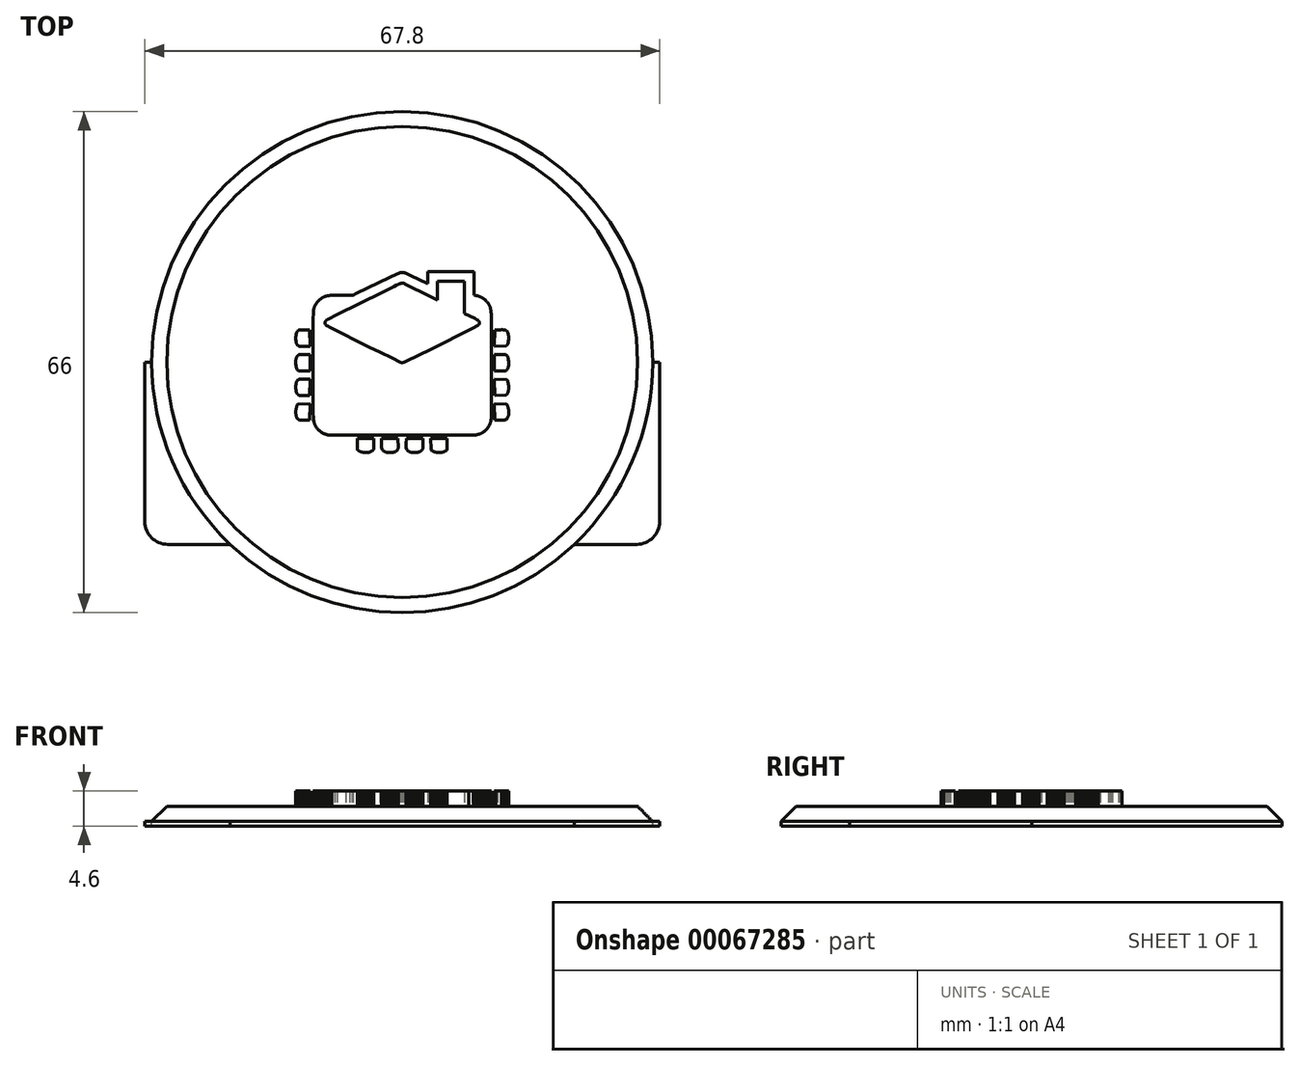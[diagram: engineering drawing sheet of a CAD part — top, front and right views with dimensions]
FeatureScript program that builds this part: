
annotation { "Feature Type Name" : "Feature", "Feature Type Description" : "" }
export const myFeature = defineFeature(function(context is Context, id is Id, definition is map)
    precondition{}
    {
        {
            var Q0;
            Q0=qCreatedBy(makeId("Top.planeOp"),FACE);
            var sketch = newSketch(context, id + "F0", { "sketchPlane" : qUnion([Q0])});
            skCircle(sketch, "E0", {"center": v(0, 0) * mm, "radius": 33 * mm});
            skLineSegment(sketch, "E1", {"start": v(0, -33) * mm, "end": v(0, -24) * mm});
            skLineSegment(sketch, "E2", {"start": v(0, -24) * mm, "end": v(33.9, -24) * mm});
            skLineSegment(sketch, "E3", {"start": v(33.9, -24) * mm, "end": v(33.9, 0) * mm});
            skLineSegment(sketch, "E4", {"start": v(33.9, 0) * mm, "end": v(33, 0) * mm});
            skLineSegment(sketch, "E5.MirrorCS", {"start": v(0, -24) * mm, "end": v(-33.9, -24) * mm});
            skLineSegment(sketch, "E6.MirrorCS", {"start": v(-33.9, 0) * mm, "end": v(-33, 0) * mm});
            skLineSegment(sketch, "E7.MirrorCS", {"start": v(-33.9, -24) * mm, "end": v(-33.9, 0) * mm});
            skSolve(sketch);
        }
        {
            var Q0;
            {var subQ0=sQuery(id+"F0.wireOp",EDGE,"E1");Q0=makeQuery(id+"F0.imprint","IMPRINT",FACE,{"disambiguationData":[TD([[makeQuery(id+"F0.imprint","IMPRINT",EDGE,{"derivedFrom":subQ0}),1.0]])]});}
            var Q1;
            {var subQ0=sQuery(id+"F0.wireOp",EDGE,"E1");Q1=makeQuery(id+"F0.imprint","IMPRINT",FACE,{"disambiguationData":[TD([[makeQuery(id+"F0.imprint","IMPRINT",EDGE,{"derivedFrom":subQ0}),-1.0]])]});}
            var Q2;
            {var subQ3=sQuery(id+"F0.wireOp",EDGE,"E0");var subQ5=makeQuery(id+"F0.imprint","INTERSECT",VERTEX,{"derivedFrom":[subQ3,sQuery(id+"F0.wireOp",EDGE,"E4")]});Q2=makeQuery(id+"F0.imprint","IMPRINT",FACE,{"disambiguationData":[TD([[makeQuery(id+"F0.imprint","IMPRINT",EDGE,{"disambiguationData":[TD([[subQ5,-1.0]])],"derivedFrom":subQ3}),1.0]])]});}
            var Q3;
            {var subQ0=sQuery(id+"F0.wireOp",EDGE,"E6.MirrorCS");Q3=makeQuery(id+"F0.imprint","IMPRINT",FACE,{"disambiguationData":[TD([[makeQuery(id+"F0.imprint","IMPRINT",EDGE,{"derivedFrom":subQ0}),-1.0]])]});}
            var Q4;
            {var subQ4=sQuery(id+"F0.wireOp",EDGE,"E3");Q4=makeQuery(id+"F0.imprint","IMPRINT",FACE,{"disambiguationData":[TD([[makeQuery(id+"F0.imprint","IMPRINT",EDGE,{"derivedFrom":subQ4}),1.0]])]});}
            extrude(context, id + "F1", {"entities" : qUnion([Q0, Q1, Q2, Q3, Q4]), "oppositeDirection" : true, "depth" : 0.6 * mm});
        }
        {
            var Q0;
            {var subQ3=sQuery(id+"F0.wireOp",EDGE,"E0");var subQ5=makeQuery(id+"F0.imprint","INTERSECT",VERTEX,{"derivedFrom":[subQ3,sQuery(id+"F0.wireOp",EDGE,"E4")]});Q0=makeQuery(id+"F0.imprint","IMPRINT",FACE,{"disambiguationData":[TD([[makeQuery(id+"F0.imprint","IMPRINT",EDGE,{"disambiguationData":[TD([[subQ5,-1.0]])],"derivedFrom":subQ3}),1.0]])]});}
            var Q1;
            {var subQ0=sQuery(id+"F0.wireOp",EDGE,"E1");Q1=makeQuery(id+"F0.imprint","IMPRINT",FACE,{"disambiguationData":[TD([[makeQuery(id+"F0.imprint","IMPRINT",EDGE,{"derivedFrom":subQ0}),1.0]])]});}
            var Q2;
            {var subQ0=sQuery(id+"F0.wireOp",EDGE,"E1");Q2=makeQuery(id+"F0.imprint","IMPRINT",FACE,{"disambiguationData":[TD([[makeQuery(id+"F0.imprint","IMPRINT",EDGE,{"derivedFrom":subQ0}),-1.0]])]});}
            extrude(context, id + "F2", {"entities" : qUnion([Q0, Q1, Q2]), "operationType" : NewBodyOperationType.ADD, "depth" : 2 * mm, "hasDraft" : true, "draftAngle" : 45 * degree, "draftPullDirection" : true});
        }
        {
            var Q0;
            Q0=qCreatedBy(makeId("Top.planeOp"),FACE);
            var sketch = newSketch(context, id + "F3", { "sketchPlane" : qUnion([Q0])});
            skLineSegment(sketch, "E8", {"start": v(3.39, 11.92) * mm, "end": v(9.43, 11.9) * mm});
            skLineSegment(sketch, "E9", {"start": v(9.43, 11.9) * mm, "end": v(9.45, 8.81) * mm});
            skLineSegment(sketch, "E10", {"start": v(9.45, 8.81) * mm, "end": v(9.52, 8.8) * mm});
            skLineSegment(sketch, "E11", {"start": v(9.52, 8.8) * mm, "end": v(9.6, 8.8) * mm});
            skLineSegment(sketch, "E12", {"start": v(9.6, 8.8) * mm, "end": v(9.66, 8.78) * mm});
            skLineSegment(sketch, "E13", {"start": v(9.66, 8.78) * mm, "end": v(9.73, 8.77) * mm});
            skLineSegment(sketch, "E14", {"start": v(9.73, 8.77) * mm, "end": v(9.8, 8.75) * mm});
            skLineSegment(sketch, "E15", {"start": v(9.8, 8.75) * mm, "end": v(9.88, 8.73) * mm});
            skLineSegment(sketch, "E16", {"start": v(9.88, 8.73) * mm, "end": v(9.95, 8.71) * mm});
            skLineSegment(sketch, "E17", {"start": v(9.95, 8.71) * mm, "end": v(10.02, 8.7) * mm});
            skLineSegment(sketch, "E18", {"start": v(10.02, 8.7) * mm, "end": v(10.08, 8.67) * mm});
            skLineSegment(sketch, "E19", {"start": v(10.08, 8.67) * mm, "end": v(10.15, 8.64) * mm});
            skLineSegment(sketch, "E20", {"start": v(10.15, 8.64) * mm, "end": v(10.22, 8.62) * mm});
            skLineSegment(sketch, "E21", {"start": v(10.22, 8.62) * mm, "end": v(10.29, 8.59) * mm});
            skLineSegment(sketch, "E22", {"start": v(10.29, 8.59) * mm, "end": v(10.35, 8.56) * mm});
            skLineSegment(sketch, "E23", {"start": v(10.35, 8.56) * mm, "end": v(10.42, 8.53) * mm});
            skLineSegment(sketch, "E24", {"start": v(10.42, 8.53) * mm, "end": v(10.48, 8.5) * mm});
            skLineSegment(sketch, "E25", {"start": v(10.48, 8.5) * mm, "end": v(10.55, 8.46) * mm});
            skLineSegment(sketch, "E26", {"start": v(10.55, 8.46) * mm, "end": v(10.6, 8.42) * mm});
            skLineSegment(sketch, "E27", {"start": v(10.6, 8.42) * mm, "end": v(10.67, 8.38) * mm});
            skLineSegment(sketch, "E28", {"start": v(10.67, 8.38) * mm, "end": v(10.73, 8.34) * mm});
            skLineSegment(sketch, "E29", {"start": v(10.73, 8.34) * mm, "end": v(10.79, 8.3) * mm});
            skLineSegment(sketch, "E30", {"start": v(10.79, 8.3) * mm, "end": v(10.85, 8.26) * mm});
            skLineSegment(sketch, "E31", {"start": v(10.85, 8.26) * mm, "end": v(10.9, 8.2) * mm});
            skLineSegment(sketch, "E32", {"start": v(10.9, 8.2) * mm, "end": v(10.95, 8.16) * mm});
            skLineSegment(sketch, "E33", {"start": v(10.95, 8.16) * mm, "end": v(11, 8.11) * mm});
            skLineSegment(sketch, "E34", {"start": v(11, 8.11) * mm, "end": v(11.06, 8.06) * mm});
            skLineSegment(sketch, "E35", {"start": v(11.06, 8.06) * mm, "end": v(11.1, 8) * mm});
            skLineSegment(sketch, "E36", {"start": v(11.1, 8) * mm, "end": v(11.15, 7.95) * mm});
            skLineSegment(sketch, "E37", {"start": v(11.15, 7.95) * mm, "end": v(11.2, 7.9) * mm});
            skLineSegment(sketch, "E38", {"start": v(11.2, 7.9) * mm, "end": v(11.24, 7.83) * mm});
            skLineSegment(sketch, "E39", {"start": v(11.24, 7.83) * mm, "end": v(11.29, 7.78) * mm});
            skLineSegment(sketch, "E40", {"start": v(11.29, 7.78) * mm, "end": v(11.33, 7.72) * mm});
            skLineSegment(sketch, "E41", {"start": v(11.33, 7.72) * mm, "end": v(11.37, 7.65) * mm});
            skLineSegment(sketch, "E42", {"start": v(11.37, 7.65) * mm, "end": v(11.41, 7.6) * mm});
            skLineSegment(sketch, "E43", {"start": v(11.41, 7.6) * mm, "end": v(11.45, 7.53) * mm});
            skLineSegment(sketch, "E44", {"start": v(11.45, 7.53) * mm, "end": v(11.48, 7.46) * mm});
            skLineSegment(sketch, "E45", {"start": v(11.48, 7.46) * mm, "end": v(11.5, 7.4) * mm});
            skLineSegment(sketch, "E46", {"start": v(11.5, 7.4) * mm, "end": v(11.53, 7.33) * mm});
            skLineSegment(sketch, "E47", {"start": v(11.53, 7.33) * mm, "end": v(11.56, 7.26) * mm});
            skLineSegment(sketch, "E48", {"start": v(11.56, 7.26) * mm, "end": v(11.58, 7.19) * mm});
            skLineSegment(sketch, "E49", {"start": v(11.58, 7.19) * mm, "end": v(11.6, 7.12) * mm});
            skLineSegment(sketch, "E50", {"start": v(11.6, 7.12) * mm, "end": v(11.62, 7.05) * mm});
            skLineSegment(sketch, "E51", {"start": v(11.62, 7.05) * mm, "end": v(11.64, 6.97) * mm});
            skLineSegment(sketch, "E52", {"start": v(11.64, 6.97) * mm, "end": v(11.65, 6.9) * mm});
            skLineSegment(sketch, "E53", {"start": v(11.65, 6.9) * mm, "end": v(11.67, 6.83) * mm});
            skLineSegment(sketch, "E54", {"start": v(11.67, 6.83) * mm, "end": v(11.68, 6.75) * mm});
            skLineSegment(sketch, "E55", {"start": v(11.68, 6.75) * mm, "end": v(11.69, 6.68) * mm});
            skLineSegment(sketch, "E56", {"start": v(11.69, 6.68) * mm, "end": v(11.7, 6.53) * mm});
            skLineSegment(sketch, "E57", {"start": v(11.7, 6.53) * mm, "end": v(11.72, 6.38) * mm});
            skLineSegment(sketch, "E58", {"start": v(11.72, 6.38) * mm, "end": v(11.72, 6.16) * mm});
            skLineSegment(sketch, "E59", {"start": v(11.72, 6.16) * mm, "end": v(11.73, 5.8) * mm});
            skLineSegment(sketch, "E60", {"start": v(11.73, 5.8) * mm, "end": v(11.72, -7.1) * mm});
            skLineSegment(sketch, "E61", {"start": v(11.72, -7.1) * mm, "end": v(11.73, -7.2) * mm});
            skLineSegment(sketch, "E62", {"start": v(11.73, -7.2) * mm, "end": v(11.73, -7.29) * mm});
            skLineSegment(sketch, "E63", {"start": v(11.73, -7.29) * mm, "end": v(11.72, -7.38) * mm});
            skLineSegment(sketch, "E64", {"start": v(11.72, -7.38) * mm, "end": v(11.72, -7.47) * mm});
            skLineSegment(sketch, "E65", {"start": v(11.72, -7.47) * mm, "end": v(11.7, -7.56) * mm});
            skLineSegment(sketch, "E66", {"start": v(11.7, -7.56) * mm, "end": v(11.69, -7.65) * mm});
            skLineSegment(sketch, "E67", {"start": v(11.69, -7.65) * mm, "end": v(11.67, -7.74) * mm});
            skLineSegment(sketch, "E68", {"start": v(11.67, -7.74) * mm, "end": v(11.65, -7.83) * mm});
            skLineSegment(sketch, "E69", {"start": v(11.65, -7.83) * mm, "end": v(11.63, -7.92) * mm});
            skLineSegment(sketch, "E70", {"start": v(11.63, -7.92) * mm, "end": v(11.6, -8) * mm});
            skLineSegment(sketch, "E71", {"start": v(11.6, -8) * mm, "end": v(11.57, -8.09) * mm});
            skLineSegment(sketch, "E72", {"start": v(11.57, -8.09) * mm, "end": v(11.53, -8.17) * mm});
            skLineSegment(sketch, "E73", {"start": v(11.53, -8.17) * mm, "end": v(11.5, -8.26) * mm});
            skLineSegment(sketch, "E74", {"start": v(11.5, -8.26) * mm, "end": v(11.45, -8.34) * mm});
            skLineSegment(sketch, "E75", {"start": v(11.45, -8.34) * mm, "end": v(11.41, -8.42) * mm});
            skLineSegment(sketch, "E76", {"start": v(11.41, -8.42) * mm, "end": v(11.37, -8.5) * mm});
            skLineSegment(sketch, "E77", {"start": v(11.37, -8.5) * mm, "end": v(11.32, -8.58) * mm});
            skLineSegment(sketch, "E78", {"start": v(11.32, -8.58) * mm, "end": v(11.26, -8.65) * mm});
            skLineSegment(sketch, "E79", {"start": v(11.26, -8.65) * mm, "end": v(11.2, -8.72) * mm});
            skLineSegment(sketch, "E80", {"start": v(11.2, -8.72) * mm, "end": v(11.15, -8.8) * mm});
            skLineSegment(sketch, "E81", {"start": v(11.15, -8.8) * mm, "end": v(11.1, -8.86) * mm});
            skLineSegment(sketch, "E82", {"start": v(11.1, -8.86) * mm, "end": v(11.03, -8.93) * mm});
            skLineSegment(sketch, "E83", {"start": v(11.03, -8.93) * mm, "end": v(10.96, -9) * mm});
            skLineSegment(sketch, "E84", {"start": v(10.96, -9) * mm, "end": v(10.9, -9.05) * mm});
            skLineSegment(sketch, "E85", {"start": v(10.9, -9.05) * mm, "end": v(10.83, -9.11) * mm});
            skLineSegment(sketch, "E86", {"start": v(10.83, -9.11) * mm, "end": v(10.75, -9.17) * mm});
            skLineSegment(sketch, "E87", {"start": v(10.75, -9.17) * mm, "end": v(10.68, -9.22) * mm});
            skLineSegment(sketch, "E88", {"start": v(10.68, -9.22) * mm, "end": v(10.6, -9.27) * mm});
            skLineSegment(sketch, "E89", {"start": v(10.6, -9.27) * mm, "end": v(10.52, -9.32) * mm});
            skLineSegment(sketch, "E90", {"start": v(10.52, -9.32) * mm, "end": v(10.47, -9.35) * mm});
            skLineSegment(sketch, "E91", {"start": v(10.47, -9.35) * mm, "end": v(10.4, -9.38) * mm});
            skLineSegment(sketch, "E92", {"start": v(10.4, -9.38) * mm, "end": v(10.35, -9.4) * mm});
            skLineSegment(sketch, "E93", {"start": v(10.35, -9.4) * mm, "end": v(10.3, -9.43) * mm});
            skLineSegment(sketch, "E94", {"start": v(10.3, -9.43) * mm, "end": v(10.23, -9.45) * mm});
            skLineSegment(sketch, "E95", {"start": v(10.23, -9.45) * mm, "end": v(10.17, -9.47) * mm});
            skLineSegment(sketch, "E96", {"start": v(10.17, -9.47) * mm, "end": v(10.11, -9.5) * mm});
            skLineSegment(sketch, "E97", {"start": v(10.11, -9.5) * mm, "end": v(10.05, -9.51) * mm});
            skLineSegment(sketch, "E98", {"start": v(10.05, -9.51) * mm, "end": v(10, -9.53) * mm});
            skLineSegment(sketch, "E99", {"start": v(10, -9.53) * mm, "end": v(9.93, -9.54) * mm});
            skLineSegment(sketch, "E100", {"start": v(9.93, -9.54) * mm, "end": v(9.87, -9.56) * mm});
            skLineSegment(sketch, "E101", {"start": v(9.87, -9.56) * mm, "end": v(9.8, -9.57) * mm});
            skLineSegment(sketch, "E102", {"start": v(9.8, -9.57) * mm, "end": v(9.68, -9.59) * mm});
            skLineSegment(sketch, "E103", {"start": v(9.68, -9.59) * mm, "end": v(9.55, -9.6) * mm});
            skLineSegment(sketch, "E104", {"start": v(9.55, -9.6) * mm, "end": v(9.36, -9.61) * mm});
            skLineSegment(sketch, "E105", {"start": v(9.36, -9.61) * mm, "end": v(8.73, -9.63) * mm});
            skLineSegment(sketch, "E106", {"start": v(8.73, -9.63) * mm, "end": v(-9.27, -9.62) * mm});
            skLineSegment(sketch, "E107", {"start": v(-9.27, -9.62) * mm, "end": v(-9.38, -9.62) * mm});
            skLineSegment(sketch, "E108", {"start": v(-9.38, -9.62) * mm, "end": v(-9.48, -9.62) * mm});
            skLineSegment(sketch, "E109", {"start": v(-9.48, -9.62) * mm, "end": v(-9.59, -9.61) * mm});
            skLineSegment(sketch, "E110", {"start": v(-9.59, -9.61) * mm, "end": v(-9.69, -9.6) * mm});
            skLineSegment(sketch, "E111", {"start": v(-9.69, -9.6) * mm, "end": v(-9.8, -9.58) * mm});
            skLineSegment(sketch, "E112", {"start": v(-9.8, -9.58) * mm, "end": v(-9.9, -9.56) * mm});
            skLineSegment(sketch, "E113", {"start": v(-9.9, -9.56) * mm, "end": v(-10, -9.54) * mm});
            skLineSegment(sketch, "E114", {"start": v(-10, -9.54) * mm, "end": v(-10.1, -9.5) * mm});
            skLineSegment(sketch, "E115", {"start": v(-10.1, -9.5) * mm, "end": v(-10.19, -9.47) * mm});
            skLineSegment(sketch, "E116", {"start": v(-10.19, -9.47) * mm, "end": v(-10.28, -9.43) * mm});
            skLineSegment(sketch, "E117", {"start": v(-10.28, -9.43) * mm, "end": v(-10.38, -9.39) * mm});
            skLineSegment(sketch, "E118", {"start": v(-10.38, -9.39) * mm, "end": v(-10.47, -9.34) * mm});
            skLineSegment(sketch, "E119", {"start": v(-10.47, -9.34) * mm, "end": v(-10.56, -9.3) * mm});
            skLineSegment(sketch, "E120", {"start": v(-10.56, -9.3) * mm, "end": v(-10.65, -9.24) * mm});
            skLineSegment(sketch, "E121", {"start": v(-10.65, -9.24) * mm, "end": v(-10.73, -9.18) * mm});
            skLineSegment(sketch, "E122", {"start": v(-10.73, -9.18) * mm, "end": v(-10.82, -9.12) * mm});
            skLineSegment(sketch, "E123", {"start": v(-10.82, -9.12) * mm, "end": v(-10.9, -9.05) * mm});
            skLineSegment(sketch, "E124", {"start": v(-10.9, -9.05) * mm, "end": v(-10.98, -8.98) * mm});
            skLineSegment(sketch, "E125", {"start": v(-10.98, -8.98) * mm, "end": v(-11.05, -8.91) * mm});
            skLineSegment(sketch, "E126", {"start": v(-11.05, -8.91) * mm, "end": v(-11.12, -8.84) * mm});
            skLineSegment(sketch, "E127", {"start": v(-11.12, -8.84) * mm, "end": v(-11.19, -8.76) * mm});
            skLineSegment(sketch, "E128", {"start": v(-11.19, -8.76) * mm, "end": v(-11.25, -8.68) * mm});
            skLineSegment(sketch, "E129", {"start": v(-11.25, -8.68) * mm, "end": v(-11.31, -8.6) * mm});
            skLineSegment(sketch, "E130", {"start": v(-11.31, -8.6) * mm, "end": v(-11.37, -8.51) * mm});
            skLineSegment(sketch, "E131", {"start": v(-11.37, -8.51) * mm, "end": v(-11.42, -8.42) * mm});
            skLineSegment(sketch, "E132", {"start": v(-11.42, -8.42) * mm, "end": v(-11.47, -8.33) * mm});
            skLineSegment(sketch, "E133", {"start": v(-11.47, -8.33) * mm, "end": v(-11.52, -8.24) * mm});
            skLineSegment(sketch, "E134", {"start": v(-11.52, -8.24) * mm, "end": v(-11.56, -8.14) * mm});
            skLineSegment(sketch, "E135", {"start": v(-11.56, -8.14) * mm, "end": v(-11.6, -8.04) * mm});
            skLineSegment(sketch, "E136", {"start": v(-11.6, -8.04) * mm, "end": v(-11.62, -7.95) * mm});
            skLineSegment(sketch, "E137", {"start": v(-11.62, -7.95) * mm, "end": v(-11.65, -7.8) * mm});
            skLineSegment(sketch, "E138", {"start": v(-11.65, -7.8) * mm, "end": v(-11.68, -7.66) * mm});
            skLineSegment(sketch, "E139", {"start": v(-11.68, -7.66) * mm, "end": v(-11.7, -7.41) * mm});
            skLineSegment(sketch, "E140", {"start": v(-11.7, -7.41) * mm, "end": v(-11.73, -6.62) * mm});
            skLineSegment(sketch, "E141", {"start": v(-11.73, -6.62) * mm, "end": v(-11.74, 5.68) * mm});
            skLineSegment(sketch, "E142", {"start": v(-11.74, 5.68) * mm, "end": v(-11.72, 6.43) * mm});
            skLineSegment(sketch, "E143", {"start": v(-11.72, 6.43) * mm, "end": v(-11.7, 6.62) * mm});
            skLineSegment(sketch, "E144", {"start": v(-11.7, 6.62) * mm, "end": v(-11.7, 6.75) * mm});
            skLineSegment(sketch, "E145", {"start": v(-11.7, 6.75) * mm, "end": v(-11.68, 6.8) * mm});
            skLineSegment(sketch, "E146", {"start": v(-11.68, 6.8) * mm, "end": v(-11.67, 6.87) * mm});
            skLineSegment(sketch, "E147", {"start": v(-11.67, 6.87) * mm, "end": v(-11.66, 6.93) * mm});
            skLineSegment(sketch, "E148", {"start": v(-11.66, 6.93) * mm, "end": v(-11.65, 7) * mm});
            skLineSegment(sketch, "E149", {"start": v(-11.65, 7) * mm, "end": v(-11.63, 7.05) * mm});
            skLineSegment(sketch, "E150", {"start": v(-11.63, 7.05) * mm, "end": v(-11.62, 7.11) * mm});
            skLineSegment(sketch, "E151", {"start": v(-11.62, 7.11) * mm, "end": v(-11.6, 7.17) * mm});
            skLineSegment(sketch, "E152", {"start": v(-11.6, 7.17) * mm, "end": v(-11.58, 7.23) * mm});
            skLineSegment(sketch, "E153", {"start": v(-11.58, 7.23) * mm, "end": v(-11.56, 7.3) * mm});
            skLineSegment(sketch, "E154", {"start": v(-11.56, 7.3) * mm, "end": v(-11.53, 7.35) * mm});
            skLineSegment(sketch, "E155", {"start": v(-11.53, 7.35) * mm, "end": v(-11.5, 7.4) * mm});
            skLineSegment(sketch, "E156", {"start": v(-11.5, 7.4) * mm, "end": v(-11.48, 7.46) * mm});
            skLineSegment(sketch, "E157", {"start": v(-11.48, 7.46) * mm, "end": v(-11.44, 7.53) * mm});
            skLineSegment(sketch, "E158", {"start": v(-11.44, 7.53) * mm, "end": v(-11.4, 7.6) * mm});
            skLineSegment(sketch, "E159", {"start": v(-11.4, 7.6) * mm, "end": v(-11.36, 7.67) * mm});
            skLineSegment(sketch, "E160", {"start": v(-11.36, 7.67) * mm, "end": v(-11.32, 7.74) * mm});
            skLineSegment(sketch, "E161", {"start": v(-11.32, 7.74) * mm, "end": v(-11.27, 7.8) * mm});
            skLineSegment(sketch, "E162", {"start": v(-11.27, 7.8) * mm, "end": v(-11.22, 7.87) * mm});
            skLineSegment(sketch, "E163", {"start": v(-11.22, 7.87) * mm, "end": v(-11.17, 7.94) * mm});
            skLineSegment(sketch, "E164", {"start": v(-11.17, 7.94) * mm, "end": v(-11.12, 8) * mm});
            skLineSegment(sketch, "E165", {"start": v(-11.12, 8) * mm, "end": v(-11.06, 8.06) * mm});
            skLineSegment(sketch, "E166", {"start": v(-11.06, 8.06) * mm, "end": v(-11, 8.11) * mm});
            skLineSegment(sketch, "E167", {"start": v(-11, 8.11) * mm, "end": v(-10.95, 8.17) * mm});
            skLineSegment(sketch, "E168", {"start": v(-10.95, 8.17) * mm, "end": v(-10.89, 8.22) * mm});
            skLineSegment(sketch, "E169", {"start": v(-10.89, 8.22) * mm, "end": v(-10.83, 8.27) * mm});
            skLineSegment(sketch, "E170", {"start": v(-10.83, 8.27) * mm, "end": v(-10.76, 8.32) * mm});
            skLineSegment(sketch, "E171", {"start": v(-10.76, 8.32) * mm, "end": v(-10.7, 8.37) * mm});
            skLineSegment(sketch, "E172", {"start": v(-10.7, 8.37) * mm, "end": v(-10.63, 8.42) * mm});
            skLineSegment(sketch, "E173", {"start": v(-10.63, 8.42) * mm, "end": v(-10.56, 8.46) * mm});
            skLineSegment(sketch, "E174", {"start": v(-10.56, 8.46) * mm, "end": v(-10.5, 8.5) * mm});
            skLineSegment(sketch, "E175", {"start": v(-10.5, 8.5) * mm, "end": v(-10.42, 8.54) * mm});
            skLineSegment(sketch, "E176", {"start": v(-10.42, 8.54) * mm, "end": v(-10.35, 8.57) * mm});
            skLineSegment(sketch, "E177", {"start": v(-10.35, 8.57) * mm, "end": v(-10.28, 8.6) * mm});
            skLineSegment(sketch, "E178", {"start": v(-10.28, 8.6) * mm, "end": v(-10.2, 8.63) * mm});
            skLineSegment(sketch, "E179", {"start": v(-10.2, 8.63) * mm, "end": v(-10.13, 8.66) * mm});
            skLineSegment(sketch, "E180", {"start": v(-10.13, 8.66) * mm, "end": v(-10.05, 8.68) * mm});
            skLineSegment(sketch, "E181", {"start": v(-10.05, 8.68) * mm, "end": v(-9.97, 8.7) * mm});
            skLineSegment(sketch, "E182", {"start": v(-9.97, 8.7) * mm, "end": v(-9.9, 8.72) * mm});
            skLineSegment(sketch, "E183", {"start": v(-9.9, 8.72) * mm, "end": v(-9.81, 8.74) * mm});
            skLineSegment(sketch, "E184", {"start": v(-9.81, 8.74) * mm, "end": v(-9.73, 8.75) * mm});
            skLineSegment(sketch, "E185", {"start": v(-9.73, 8.75) * mm, "end": v(-9.65, 8.76) * mm});
            skLineSegment(sketch, "E186", {"start": v(-9.65, 8.76) * mm, "end": v(-9.44, 8.77) * mm});
            skLineSegment(sketch, "E187", {"start": v(-9.44, 8.77) * mm, "end": v(-9.24, 8.79) * mm});
            skLineSegment(sketch, "E188", {"start": v(-9.24, 8.79) * mm, "end": v(-8.92, 8.8) * mm});
            skLineSegment(sketch, "E189", {"start": v(-8.92, 8.8) * mm, "end": v(-7.46, 8.79) * mm});
            skLineSegment(sketch, "E190", {"start": v(-7.46, 8.79) * mm, "end": v(-6.94, 8.8) * mm});
            skLineSegment(sketch, "E191", {"start": v(-6.94, 8.8) * mm, "end": v(-6.63, 8.8) * mm});
            skLineSegment(sketch, "E192", {"start": v(-6.63, 8.8) * mm, "end": v(-6.5, 8.83) * mm});
            skLineSegment(sketch, "E193", {"start": v(-6.5, 8.83) * mm, "end": v(-6.03, 9.03) * mm});
            skLineSegment(sketch, "E194", {"start": v(-6.03, 9.03) * mm, "end": v(-1.65, 11.14) * mm});
            skLineSegment(sketch, "E195", {"start": v(-1.65, 11.14) * mm, "end": v(-0.7, 11.6) * mm});
            skLineSegment(sketch, "E196", {"start": v(-0.7, 11.6) * mm, "end": v(-0.5, 11.68) * mm});
            skLineSegment(sketch, "E197", {"start": v(-0.5, 11.68) * mm, "end": v(-0.36, 11.74) * mm});
            skLineSegment(sketch, "E198", {"start": v(-0.36, 11.74) * mm, "end": v(-0.25, 11.77) * mm});
            skLineSegment(sketch, "E199", {"start": v(-0.25, 11.77) * mm, "end": v(-0.2, 11.77) * mm});
            skLineSegment(sketch, "E200", {"start": v(-0.2, 11.77) * mm, "end": v(-0.16, 11.78) * mm});
            skLineSegment(sketch, "E201", {"start": v(-0.16, 11.78) * mm, "end": v(-0.11, 11.79) * mm});
            skLineSegment(sketch, "E202", {"start": v(-0.11, 11.79) * mm, "end": v(-0.06, 11.8) * mm});
            skLineSegment(sketch, "E203", {"start": v(-0.06, 11.8) * mm, "end": v(-0.02, 11.8) * mm});
            skLineSegment(sketch, "E204", {"start": v(-0.02, 11.8) * mm, "end": v(0.03, 11.8) * mm});
            skLineSegment(sketch, "E205", {"start": v(0.03, 11.8) * mm, "end": v(0.08, 11.79) * mm});
            skLineSegment(sketch, "E206", {"start": v(0.08, 11.79) * mm, "end": v(0.12, 11.78) * mm});
            skLineSegment(sketch, "E207", {"start": v(0.12, 11.78) * mm, "end": v(0.17, 11.78) * mm});
            skLineSegment(sketch, "E208", {"start": v(0.17, 11.78) * mm, "end": v(0.22, 11.77) * mm});
            skLineSegment(sketch, "E209", {"start": v(0.22, 11.77) * mm, "end": v(0.26, 11.76) * mm});
            skLineSegment(sketch, "E210", {"start": v(0.26, 11.76) * mm, "end": v(0.35, 11.73) * mm});
            skLineSegment(sketch, "E211", {"start": v(0.35, 11.73) * mm, "end": v(0.44, 11.7) * mm});
            skLineSegment(sketch, "E212", {"start": v(0.44, 11.7) * mm, "end": v(0.58, 11.66) * mm});
            skLineSegment(sketch, "E213", {"start": v(0.58, 11.66) * mm, "end": v(1.05, 11.44) * mm});
            skLineSegment(sketch, "E214", {"start": v(1.05, 11.44) * mm, "end": v(3.39, 10.3) * mm});
            skLineSegment(sketch, "E215", {"start": v(3.39, 10.3) * mm, "end": v(3.39, 11.92) * mm});
            skLineSegment(sketch, "E216", {"start": v(4.65, 10.66) * mm, "end": v(4.64, 8.2) * mm});
            skLineSegment(sketch, "E217", {"start": v(4.64, 8.2) * mm, "end": v(4.5, 8.26) * mm});
            skLineSegment(sketch, "E218", {"start": v(4.5, 8.26) * mm, "end": v(3.6, 8.68) * mm});
            skLineSegment(sketch, "E219", {"start": v(3.6, 8.68) * mm, "end": v(0.39, 10.3) * mm});
            skLineSegment(sketch, "E220", {"start": v(0.39, 10.3) * mm, "end": v(0.35, 10.32) * mm});
            skLineSegment(sketch, "E221", {"start": v(0.35, 10.32) * mm, "end": v(0.3, 10.34) * mm});
            skLineSegment(sketch, "E222", {"start": v(0.3, 10.34) * mm, "end": v(0.27, 10.35) * mm});
            skLineSegment(sketch, "E223", {"start": v(0.27, 10.35) * mm, "end": v(0.23, 10.37) * mm});
            skLineSegment(sketch, "E224", {"start": v(0.23, 10.37) * mm, "end": v(0.19, 10.38) * mm});
            skLineSegment(sketch, "E225", {"start": v(0.19, 10.38) * mm, "end": v(0.15, 10.39) * mm});
            skLineSegment(sketch, "E226", {"start": v(0.15, 10.39) * mm, "end": v(0.1, 10.4) * mm});
            skLineSegment(sketch, "E227", {"start": v(0.1, 10.4) * mm, "end": v(0.07, 10.4) * mm});
            skLineSegment(sketch, "E228", {"start": v(0.07, 10.4) * mm, "end": v(0.03, 10.4) * mm});
            skLineSegment(sketch, "E229", {"start": v(0.03, 10.4) * mm, "end": v(-0.02, 10.4) * mm});
            skLineSegment(sketch, "E230", {"start": v(-0.02, 10.4) * mm, "end": v(-0.06, 10.4) * mm});
            skLineSegment(sketch, "E231", {"start": v(-0.06, 10.4) * mm, "end": v(-0.1, 10.39) * mm});
            skLineSegment(sketch, "E232", {"start": v(-0.1, 10.39) * mm, "end": v(-0.14, 10.38) * mm});
            skLineSegment(sketch, "E233", {"start": v(-0.14, 10.38) * mm, "end": v(-0.18, 10.37) * mm});
            skLineSegment(sketch, "E234", {"start": v(-0.18, 10.37) * mm, "end": v(-0.22, 10.36) * mm});
            skLineSegment(sketch, "E235", {"start": v(-0.22, 10.36) * mm, "end": v(-0.26, 10.35) * mm});
            skLineSegment(sketch, "E236", {"start": v(-0.26, 10.35) * mm, "end": v(-0.34, 10.32) * mm});
            skLineSegment(sketch, "E237", {"start": v(-0.34, 10.32) * mm, "end": v(-0.46, 10.27) * mm});
            skLineSegment(sketch, "E238", {"start": v(-0.46, 10.27) * mm, "end": v(-0.76, 10.12) * mm});
            skLineSegment(sketch, "E239", {"start": v(-0.76, 10.12) * mm, "end": v(-1.07, 9.96) * mm});
            skLineSegment(sketch, "E240", {"start": v(-1.07, 9.96) * mm, "end": v(-2.62, 9.18) * mm});
            skLineSegment(sketch, "E241", {"start": v(-2.62, 9.18) * mm, "end": v(-8.57, 6.24) * mm});
            skLineSegment(sketch, "E242", {"start": v(-8.57, 6.24) * mm, "end": v(-9.81, 5.61) * mm});
            skLineSegment(sketch, "E243", {"start": v(-9.81, 5.61) * mm, "end": v(-9.88, 5.58) * mm});
            skLineSegment(sketch, "E244", {"start": v(-9.88, 5.58) * mm, "end": v(-9.95, 5.54) * mm});
            skLineSegment(sketch, "E245", {"start": v(-9.95, 5.54) * mm, "end": v(-10, 5.5) * mm});
            skLineSegment(sketch, "E246", {"start": v(-10, 5.5) * mm, "end": v(-10.05, 5.46) * mm});
            skLineSegment(sketch, "E247", {"start": v(-10.05, 5.46) * mm, "end": v(-10.08, 5.42) * mm});
            skLineSegment(sketch, "E248", {"start": v(-10.08, 5.42) * mm, "end": v(-10.11, 5.38) * mm});
            skLineSegment(sketch, "E249", {"start": v(-10.11, 5.38) * mm, "end": v(-10.13, 5.36) * mm});
            skLineSegment(sketch, "E250", {"start": v(-10.13, 5.36) * mm, "end": v(-10.14, 5.34) * mm});
            skLineSegment(sketch, "E251", {"start": v(-10.14, 5.34) * mm, "end": v(-10.15, 5.32) * mm});
            skLineSegment(sketch, "E252", {"start": v(-10.15, 5.32) * mm, "end": v(-10.16, 5.3) * mm});
            skLineSegment(sketch, "E253", {"start": v(-10.16, 5.3) * mm, "end": v(-10.17, 5.27) * mm});
            skLineSegment(sketch, "E254", {"start": v(-10.17, 5.27) * mm, "end": v(-10.17, 5.25) * mm});
            skLineSegment(sketch, "E255", {"start": v(-10.17, 5.25) * mm, "end": v(-10.18, 5.22) * mm});
            skLineSegment(sketch, "E256", {"start": v(-10.18, 5.22) * mm, "end": v(-10.18, 5.2) * mm});
            skLineSegment(sketch, "E257", {"start": v(-10.18, 5.2) * mm, "end": v(-10.18, 5.17) * mm});
            skLineSegment(sketch, "E258", {"start": v(-10.18, 5.17) * mm, "end": v(-10.18, 5.15) * mm});
            skLineSegment(sketch, "E259", {"start": v(-10.18, 5.15) * mm, "end": v(-10.18, 5.12) * mm});
            skLineSegment(sketch, "E260", {"start": v(-10.18, 5.12) * mm, "end": v(-10.17, 5.1) * mm});
            skLineSegment(sketch, "E261", {"start": v(-10.17, 5.1) * mm, "end": v(-10.16, 5.07) * mm});
            skLineSegment(sketch, "E262", {"start": v(-10.16, 5.07) * mm, "end": v(-10.15, 5.04) * mm});
            skLineSegment(sketch, "E263", {"start": v(-10.15, 5.04) * mm, "end": v(-10.14, 5.01) * mm});
            skLineSegment(sketch, "E264", {"start": v(-10.14, 5.01) * mm, "end": v(-10.13, 4.99) * mm});
            skLineSegment(sketch, "E265", {"start": v(-10.13, 4.99) * mm, "end": v(-10.12, 4.97) * mm});
            skLineSegment(sketch, "E266", {"start": v(-10.12, 4.97) * mm, "end": v(-10.1, 4.94) * mm});
            skLineSegment(sketch, "E267", {"start": v(-10.1, 4.94) * mm, "end": v(-10.1, 4.92) * mm});
            skLineSegment(sketch, "E268", {"start": v(-10.1, 4.92) * mm, "end": v(-10.08, 4.9) * mm});
            skLineSegment(sketch, "E269", {"start": v(-10.08, 4.9) * mm, "end": v(-10.04, 4.87) * mm});
            skLineSegment(sketch, "E270", {"start": v(-10.04, 4.87) * mm, "end": v(-10, 4.83) * mm});
            skLineSegment(sketch, "E271", {"start": v(-10, 4.83) * mm, "end": v(-9.96, 4.8) * mm});
            skLineSegment(sketch, "E272", {"start": v(-9.96, 4.8) * mm, "end": v(-9.8, 4.71) * mm});
            skLineSegment(sketch, "E273", {"start": v(-9.8, 4.71) * mm, "end": v(-9.58, 4.6) * mm});
            skLineSegment(sketch, "E274", {"start": v(-9.58, 4.6) * mm, "end": v(-4.3, 1.96) * mm});
            skLineSegment(sketch, "E275", {"start": v(-4.3, 1.96) * mm, "end": v(-2.91, 1.3) * mm});
            skLineSegment(sketch, "E276", {"start": v(-2.91, 1.3) * mm, "end": v(-1.37, 0.52) * mm});
            skLineSegment(sketch, "E277", {"start": v(-1.37, 0.52) * mm, "end": v(-0.27, -0.01) * mm});
            skLineSegment(sketch, "E278", {"start": v(-0.27, -0.01) * mm, "end": v(-0.24, -0.03) * mm});
            skLineSegment(sketch, "E279", {"start": v(-0.24, -0.03) * mm, "end": v(-0.22, -0.04) * mm});
            skLineSegment(sketch, "E280", {"start": v(-0.22, -0.04) * mm, "end": v(-0.19, -0.05) * mm});
            skLineSegment(sketch, "E281", {"start": v(-0.19, -0.05) * mm, "end": v(-0.16, -0.06) * mm});
            skLineSegment(sketch, "E282", {"start": v(-0.16, -0.06) * mm, "end": v(-0.14, -0.06) * mm});
            skLineSegment(sketch, "E283", {"start": v(-0.14, -0.06) * mm, "end": v(-0.1, -0.07) * mm});
            skLineSegment(sketch, "E284", {"start": v(-0.1, -0.07) * mm, "end": v(-0.08, -0.07) * mm});
            skLineSegment(sketch, "E285", {"start": v(-0.08, -0.07) * mm, "end": v(-0.05, -0.07) * mm});
            skLineSegment(sketch, "E286", {"start": v(-0.05, -0.07) * mm, "end": v(-0.03, -0.07) * mm});
            skLineSegment(sketch, "E287", {"start": v(-0.03, -0.07) * mm, "end": v(0.03, -0.07) * mm});
            skLineSegment(sketch, "E288", {"start": v(0.03, -0.07) * mm, "end": v(0.08, -0.06) * mm});
            skLineSegment(sketch, "E289", {"start": v(0.08, -0.06) * mm, "end": v(0.14, -0.05) * mm});
            skLineSegment(sketch, "E290", {"start": v(0.14, -0.05) * mm, "end": v(0.25, -0.02) * mm});
            skLineSegment(sketch, "E291", {"start": v(0.25, -0.02) * mm, "end": v(0.5, 0.1) * mm});
            skLineSegment(sketch, "E292", {"start": v(0.5, 0.1) * mm, "end": v(3.8, 1.72) * mm});
            skLineSegment(sketch, "E293", {"start": v(3.8, 1.72) * mm, "end": v(9.2, 4.41) * mm});
            skLineSegment(sketch, "E294", {"start": v(9.2, 4.41) * mm, "end": v(10.03, 4.86) * mm});
            skLineSegment(sketch, "E295", {"start": v(10.03, 4.86) * mm, "end": v(10.04, 4.87) * mm});
            skLineSegment(sketch, "E296", {"start": v(10.04, 4.87) * mm, "end": v(10.06, 4.9) * mm});
            skLineSegment(sketch, "E297", {"start": v(10.06, 4.9) * mm, "end": v(10.08, 4.9) * mm});
            skLineSegment(sketch, "E298", {"start": v(10.08, 4.9) * mm, "end": v(10.1, 4.93) * mm});
            skLineSegment(sketch, "E299", {"start": v(10.1, 4.93) * mm, "end": v(10.1, 4.95) * mm});
            skLineSegment(sketch, "E300", {"start": v(10.1, 4.95) * mm, "end": v(10.12, 4.97) * mm});
            skLineSegment(sketch, "E301", {"start": v(10.12, 4.97) * mm, "end": v(10.13, 4.99) * mm});
            skLineSegment(sketch, "E302", {"start": v(10.13, 4.99) * mm, "end": v(10.14, 5.01) * mm});
            skLineSegment(sketch, "E303", {"start": v(10.14, 5.01) * mm, "end": v(10.15, 5.03) * mm});
            skLineSegment(sketch, "E304", {"start": v(10.15, 5.03) * mm, "end": v(10.15, 5.06) * mm});
            skLineSegment(sketch, "E305", {"start": v(10.15, 5.06) * mm, "end": v(10.16, 5.08) * mm});
            skLineSegment(sketch, "E306", {"start": v(10.16, 5.08) * mm, "end": v(10.16, 5.1) * mm});
            skLineSegment(sketch, "E307", {"start": v(10.16, 5.1) * mm, "end": v(10.17, 5.13) * mm});
            skLineSegment(sketch, "E308", {"start": v(10.17, 5.13) * mm, "end": v(10.17, 5.15) * mm});
            skLineSegment(sketch, "E309", {"start": v(10.17, 5.15) * mm, "end": v(10.17, 5.2) * mm});
            skLineSegment(sketch, "E310", {"start": v(10.17, 5.2) * mm, "end": v(10.16, 5.23) * mm});
            skLineSegment(sketch, "E311", {"start": v(10.16, 5.23) * mm, "end": v(10.16, 5.25) * mm});
            skLineSegment(sketch, "E312", {"start": v(10.16, 5.25) * mm, "end": v(10.15, 5.28) * mm});
            skLineSegment(sketch, "E313", {"start": v(10.15, 5.28) * mm, "end": v(10.15, 5.3) * mm});
            skLineSegment(sketch, "E314", {"start": v(10.15, 5.3) * mm, "end": v(10.14, 5.32) * mm});
            skLineSegment(sketch, "E315", {"start": v(10.14, 5.32) * mm, "end": v(10.13, 5.34) * mm});
            skLineSegment(sketch, "E316", {"start": v(10.13, 5.34) * mm, "end": v(10.12, 5.37) * mm});
            skLineSegment(sketch, "E317", {"start": v(10.12, 5.37) * mm, "end": v(10.1, 5.39) * mm});
            skLineSegment(sketch, "E318", {"start": v(10.1, 5.39) * mm, "end": v(10.1, 5.4) * mm});
            skLineSegment(sketch, "E319", {"start": v(10.1, 5.4) * mm, "end": v(10.08, 5.42) * mm});
            skLineSegment(sketch, "E320", {"start": v(10.08, 5.42) * mm, "end": v(10.06, 5.44) * mm});
            skLineSegment(sketch, "E321", {"start": v(10.06, 5.44) * mm, "end": v(10.04, 5.46) * mm});
            skLineSegment(sketch, "E322", {"start": v(10.04, 5.46) * mm, "end": v(10.03, 5.47) * mm});
            skLineSegment(sketch, "E323", {"start": v(10.03, 5.47) * mm, "end": v(9.84, 5.59) * mm});
            skLineSegment(sketch, "E324", {"start": v(9.84, 5.59) * mm, "end": v(9.6, 5.73) * mm});
            skLineSegment(sketch, "E325", {"start": v(9.6, 5.73) * mm, "end": v(8.2, 6.4) * mm});
            skLineSegment(sketch, "E326", {"start": v(8.2, 6.4) * mm, "end": v(8.19, 10.66) * mm});
            skLineSegment(sketch, "E327", {"start": v(8.19, 10.66) * mm, "end": v(4.65, 10.66) * mm});
            skLineSegment(sketch, "E328", {"start": v(-13.63, 4.2) * mm, "end": v(-12.17, 4.23) * mm});
            skLineSegment(sketch, "E329", {"start": v(-12.17, 4.23) * mm, "end": v(-12.15, 2.07) * mm});
            skLineSegment(sketch, "E330", {"start": v(-12.15, 2.07) * mm, "end": v(-13.3, 2.08) * mm});
            skLineSegment(sketch, "E331", {"start": v(-13.3, 2.08) * mm, "end": v(-13.52, 2.1) * mm});
            skLineSegment(sketch, "E332", {"start": v(-13.52, 2.1) * mm, "end": v(-13.67, 2.12) * mm});
            skLineSegment(sketch, "E333", {"start": v(-13.67, 2.12) * mm, "end": v(-13.7, 2.15) * mm});
            skLineSegment(sketch, "E334", {"start": v(-13.7, 2.15) * mm, "end": v(-13.74, 2.17) * mm});
            skLineSegment(sketch, "E335", {"start": v(-13.74, 2.17) * mm, "end": v(-13.77, 2.2) * mm});
            skLineSegment(sketch, "E336", {"start": v(-13.77, 2.2) * mm, "end": v(-13.8, 2.23) * mm});
            skLineSegment(sketch, "E337", {"start": v(-13.8, 2.23) * mm, "end": v(-13.82, 2.26) * mm});
            skLineSegment(sketch, "E338", {"start": v(-13.82, 2.26) * mm, "end": v(-13.85, 2.3) * mm});
            skLineSegment(sketch, "E339", {"start": v(-13.85, 2.3) * mm, "end": v(-13.87, 2.33) * mm});
            skLineSegment(sketch, "E340", {"start": v(-13.87, 2.33) * mm, "end": v(-13.9, 2.36) * mm});
            skLineSegment(sketch, "E341", {"start": v(-13.9, 2.36) * mm, "end": v(-13.9, 2.4) * mm});
            skLineSegment(sketch, "E342", {"start": v(-13.9, 2.4) * mm, "end": v(-13.92, 2.44) * mm});
            skLineSegment(sketch, "E343", {"start": v(-13.92, 2.44) * mm, "end": v(-13.94, 2.48) * mm});
            skLineSegment(sketch, "E344", {"start": v(-13.94, 2.48) * mm, "end": v(-13.95, 2.52) * mm});
            skLineSegment(sketch, "E345", {"start": v(-13.95, 2.52) * mm, "end": v(-13.96, 2.56) * mm});
            skLineSegment(sketch, "E346", {"start": v(-13.96, 2.56) * mm, "end": v(-13.97, 2.6) * mm});
            skLineSegment(sketch, "E347", {"start": v(-13.97, 2.6) * mm, "end": v(-13.99, 2.68) * mm});
            skLineSegment(sketch, "E348", {"start": v(-13.99, 2.68) * mm, "end": v(-14, 2.76) * mm});
            skLineSegment(sketch, "E349", {"start": v(-14, 2.76) * mm, "end": v(-14.01, 2.93) * mm});
            skLineSegment(sketch, "E350", {"start": v(-14.01, 2.93) * mm, "end": v(-14.02, 3.14) * mm});
            skLineSegment(sketch, "E351", {"start": v(-14.02, 3.14) * mm, "end": v(-14.02, 3.22) * mm});
            skLineSegment(sketch, "E352", {"start": v(-14.02, 3.22) * mm, "end": v(-14.02, 3.33) * mm});
            skLineSegment(sketch, "E353", {"start": v(-14.02, 3.33) * mm, "end": v(-14, 3.48) * mm});
            skLineSegment(sketch, "E354", {"start": v(-14, 3.48) * mm, "end": v(-13.99, 3.6) * mm});
            skLineSegment(sketch, "E355", {"start": v(-13.99, 3.6) * mm, "end": v(-13.98, 3.68) * mm});
            skLineSegment(sketch, "E356", {"start": v(-13.98, 3.68) * mm, "end": v(-13.96, 3.76) * mm});
            skLineSegment(sketch, "E357", {"start": v(-13.96, 3.76) * mm, "end": v(-13.95, 3.8) * mm});
            skLineSegment(sketch, "E358", {"start": v(-13.95, 3.8) * mm, "end": v(-13.93, 3.83) * mm});
            skLineSegment(sketch, "E359", {"start": v(-13.93, 3.83) * mm, "end": v(-13.92, 3.87) * mm});
            skLineSegment(sketch, "E360", {"start": v(-13.92, 3.87) * mm, "end": v(-13.9, 3.9) * mm});
            skLineSegment(sketch, "E361", {"start": v(-13.9, 3.9) * mm, "end": v(-13.89, 3.94) * mm});
            skLineSegment(sketch, "E362", {"start": v(-13.89, 3.94) * mm, "end": v(-13.87, 3.97) * mm});
            skLineSegment(sketch, "E363", {"start": v(-13.87, 3.97) * mm, "end": v(-13.85, 4) * mm});
            skLineSegment(sketch, "E364", {"start": v(-13.85, 4) * mm, "end": v(-13.83, 4.03) * mm});
            skLineSegment(sketch, "E365", {"start": v(-13.83, 4.03) * mm, "end": v(-13.8, 4.06) * mm});
            skLineSegment(sketch, "E366", {"start": v(-13.8, 4.06) * mm, "end": v(-13.78, 4.1) * mm});
            skLineSegment(sketch, "E367", {"start": v(-13.78, 4.1) * mm, "end": v(-13.75, 4.12) * mm});
            skLineSegment(sketch, "E368", {"start": v(-13.75, 4.12) * mm, "end": v(-13.72, 4.14) * mm});
            skLineSegment(sketch, "E369", {"start": v(-13.72, 4.14) * mm, "end": v(-13.7, 4.17) * mm});
            skLineSegment(sketch, "E370", {"start": v(-13.7, 4.17) * mm, "end": v(-13.66, 4.19) * mm});
            skLineSegment(sketch, "E371", {"start": v(-13.66, 4.19) * mm, "end": v(-13.63, 4.2) * mm});
            skLineSegment(sketch, "E372", {"start": v(12.16, 4.22) * mm, "end": v(12.22, 4.21) * mm});
            skLineSegment(sketch, "E373", {"start": v(12.22, 4.21) * mm, "end": v(12.28, 4.21) * mm});
            skLineSegment(sketch, "E374", {"start": v(12.28, 4.21) * mm, "end": v(12.34, 4.2) * mm});
            skLineSegment(sketch, "E375", {"start": v(12.34, 4.2) * mm, "end": v(12.4, 4.2) * mm});
            skLineSegment(sketch, "E376", {"start": v(12.4, 4.2) * mm, "end": v(12.46, 4.21) * mm});
            skLineSegment(sketch, "E377", {"start": v(12.46, 4.21) * mm, "end": v(12.59, 4.22) * mm});
            skLineSegment(sketch, "E378", {"start": v(12.59, 4.22) * mm, "end": v(12.98, 4.26) * mm});
            skLineSegment(sketch, "E379", {"start": v(12.98, 4.26) * mm, "end": v(13.04, 4.26) * mm});
            skLineSegment(sketch, "E380", {"start": v(13.04, 4.26) * mm, "end": v(13.1, 4.27) * mm});
            skLineSegment(sketch, "E381", {"start": v(13.1, 4.27) * mm, "end": v(13.17, 4.27) * mm});
            skLineSegment(sketch, "E382", {"start": v(13.17, 4.27) * mm, "end": v(13.23, 4.27) * mm});
            skLineSegment(sketch, "E383", {"start": v(13.23, 4.27) * mm, "end": v(13.3, 4.26) * mm});
            skLineSegment(sketch, "E384", {"start": v(13.3, 4.26) * mm, "end": v(13.35, 4.26) * mm});
            skLineSegment(sketch, "E385", {"start": v(13.35, 4.26) * mm, "end": v(13.41, 4.25) * mm});
            skLineSegment(sketch, "E386", {"start": v(13.41, 4.25) * mm, "end": v(13.47, 4.24) * mm});
            skLineSegment(sketch, "E387", {"start": v(13.47, 4.24) * mm, "end": v(13.53, 4.22) * mm});
            skLineSegment(sketch, "E388", {"start": v(13.53, 4.22) * mm, "end": v(13.58, 4.2) * mm});
            skLineSegment(sketch, "E389", {"start": v(13.58, 4.2) * mm, "end": v(13.64, 4.18) * mm});
            skLineSegment(sketch, "E390", {"start": v(13.64, 4.18) * mm, "end": v(13.69, 4.15) * mm});
            skLineSegment(sketch, "E391", {"start": v(13.69, 4.15) * mm, "end": v(13.74, 4.12) * mm});
            skLineSegment(sketch, "E392", {"start": v(13.74, 4.12) * mm, "end": v(13.79, 4.08) * mm});
            skLineSegment(sketch, "E393", {"start": v(13.79, 4.08) * mm, "end": v(13.83, 4.03) * mm});
            skLineSegment(sketch, "E394", {"start": v(13.83, 4.03) * mm, "end": v(13.87, 3.98) * mm});
            skLineSegment(sketch, "E395", {"start": v(13.87, 3.98) * mm, "end": v(13.9, 3.94) * mm});
            skLineSegment(sketch, "E396", {"start": v(13.9, 3.94) * mm, "end": v(13.9, 3.9) * mm});
            skLineSegment(sketch, "E397", {"start": v(13.9, 3.9) * mm, "end": v(13.92, 3.85) * mm});
            skLineSegment(sketch, "E398", {"start": v(13.92, 3.85) * mm, "end": v(13.95, 3.75) * mm});
            skLineSegment(sketch, "E399", {"start": v(13.95, 3.75) * mm, "end": v(13.97, 3.66) * mm});
            skLineSegment(sketch, "E400", {"start": v(13.97, 3.66) * mm, "end": v(13.99, 3.56) * mm});
            skLineSegment(sketch, "E401", {"start": v(13.99, 3.56) * mm, "end": v(14, 3.47) * mm});
            skLineSegment(sketch, "E402", {"start": v(14, 3.47) * mm, "end": v(14, 3.37) * mm});
            skLineSegment(sketch, "E403", {"start": v(14, 3.37) * mm, "end": v(14.01, 3.22) * mm});
            skLineSegment(sketch, "E404", {"start": v(14.01, 3.22) * mm, "end": v(14, 3.03) * mm});
            skLineSegment(sketch, "E405", {"start": v(14, 3.03) * mm, "end": v(13.98, 2.7) * mm});
            skLineSegment(sketch, "E406", {"start": v(13.98, 2.7) * mm, "end": v(13.97, 2.6) * mm});
            skLineSegment(sketch, "E407", {"start": v(13.97, 2.6) * mm, "end": v(13.9, 2.4) * mm});
            skLineSegment(sketch, "E408", {"start": v(13.9, 2.4) * mm, "end": v(13.85, 2.3) * mm});
            skLineSegment(sketch, "E409", {"start": v(13.85, 2.3) * mm, "end": v(13.8, 2.24) * mm});
            skLineSegment(sketch, "E410", {"start": v(13.8, 2.24) * mm, "end": v(13.77, 2.2) * mm});
            skLineSegment(sketch, "E411", {"start": v(13.77, 2.2) * mm, "end": v(13.73, 2.17) * mm});
            skLineSegment(sketch, "E412", {"start": v(13.73, 2.17) * mm, "end": v(13.7, 2.14) * mm});
            skLineSegment(sketch, "E413", {"start": v(13.7, 2.14) * mm, "end": v(13.66, 2.12) * mm});
            skLineSegment(sketch, "E414", {"start": v(13.66, 2.12) * mm, "end": v(13.62, 2.1) * mm});
            skLineSegment(sketch, "E415", {"start": v(13.62, 2.1) * mm, "end": v(12.14, 2.07) * mm});
            skLineSegment(sketch, "E416", {"start": v(12.14, 2.07) * mm, "end": v(12.16, 4.22) * mm});
            skLineSegment(sketch, "E417", {"start": v(-13.64, 0.97) * mm, "end": v(-12.15, 1) * mm});
            skLineSegment(sketch, "E418", {"start": v(-12.15, 1) * mm, "end": v(-12.15, -1.17) * mm});
            skLineSegment(sketch, "E419", {"start": v(-12.15, -1.17) * mm, "end": v(-13.64, -1.14) * mm});
            skLineSegment(sketch, "E420", {"start": v(-13.64, -1.14) * mm, "end": v(-13.83, -0.95) * mm});
            skLineSegment(sketch, "E421", {"start": v(-13.83, -0.95) * mm, "end": v(-13.9, -0.83) * mm});
            skLineSegment(sketch, "E422", {"start": v(-13.9, -0.83) * mm, "end": v(-13.94, -0.75) * mm});
            skLineSegment(sketch, "E423", {"start": v(-13.94, -0.75) * mm, "end": v(-13.97, -0.69) * mm});
            skLineSegment(sketch, "E424", {"start": v(-13.97, -0.69) * mm, "end": v(-13.98, -0.62) * mm});
            skLineSegment(sketch, "E425", {"start": v(-13.98, -0.62) * mm, "end": v(-13.98, -0.6) * mm});
            skLineSegment(sketch, "E426", {"start": v(-13.98, -0.6) * mm, "end": v(-14, -0.49) * mm});
            skLineSegment(sketch, "E427", {"start": v(-14, -0.49) * mm, "end": v(-14.02, -0.25) * mm});
            skLineSegment(sketch, "E428", {"start": v(-14.02, -0.25) * mm, "end": v(-14.03, -0.08) * mm});
            skLineSegment(sketch, "E429", {"start": v(-14.03, -0.08) * mm, "end": v(-14.03, 0.04) * mm});
            skLineSegment(sketch, "E430", {"start": v(-14.03, 0.04) * mm, "end": v(-14.03, 0.1) * mm});
            skLineSegment(sketch, "E431", {"start": v(-14.03, 0.1) * mm, "end": v(-14.03, 0.16) * mm});
            skLineSegment(sketch, "E432", {"start": v(-14.03, 0.16) * mm, "end": v(-14.02, 0.22) * mm});
            skLineSegment(sketch, "E433", {"start": v(-14.02, 0.22) * mm, "end": v(-14.02, 0.28) * mm});
            skLineSegment(sketch, "E434", {"start": v(-14.02, 0.28) * mm, "end": v(-14, 0.34) * mm});
            skLineSegment(sketch, "E435", {"start": v(-14, 0.34) * mm, "end": v(-14, 0.4) * mm});
            skLineSegment(sketch, "E436", {"start": v(-14, 0.4) * mm, "end": v(-13.98, 0.45) * mm});
            skLineSegment(sketch, "E437", {"start": v(-13.98, 0.45) * mm, "end": v(-13.97, 0.5) * mm});
            skLineSegment(sketch, "E438", {"start": v(-13.97, 0.5) * mm, "end": v(-13.95, 0.56) * mm});
            skLineSegment(sketch, "E439", {"start": v(-13.95, 0.56) * mm, "end": v(-13.93, 0.61) * mm});
            skLineSegment(sketch, "E440", {"start": v(-13.93, 0.61) * mm, "end": v(-13.9, 0.66) * mm});
            skLineSegment(sketch, "E441", {"start": v(-13.9, 0.66) * mm, "end": v(-13.88, 0.71) * mm});
            skLineSegment(sketch, "E442", {"start": v(-13.88, 0.71) * mm, "end": v(-13.85, 0.76) * mm});
            skLineSegment(sketch, "E443", {"start": v(-13.85, 0.76) * mm, "end": v(-13.81, 0.8) * mm});
            skLineSegment(sketch, "E444", {"start": v(-13.81, 0.8) * mm, "end": v(-13.78, 0.85) * mm});
            skLineSegment(sketch, "E445", {"start": v(-13.78, 0.85) * mm, "end": v(-13.73, 0.9) * mm});
            skLineSegment(sketch, "E446", {"start": v(-13.73, 0.9) * mm, "end": v(-13.69, 0.94) * mm});
            skLineSegment(sketch, "E447", {"start": v(-13.69, 0.94) * mm, "end": v(-13.64, 0.97) * mm});
            skLineSegment(sketch, "E448", {"start": v(12.14, 1) * mm, "end": v(13.63, 0.97) * mm});
            skLineSegment(sketch, "E449", {"start": v(13.63, 0.97) * mm, "end": v(13.8, 0.8) * mm});
            skLineSegment(sketch, "E450", {"start": v(13.8, 0.8) * mm, "end": v(13.89, 0.69) * mm});
            skLineSegment(sketch, "E451", {"start": v(13.89, 0.69) * mm, "end": v(13.93, 0.6) * mm});
            skLineSegment(sketch, "E452", {"start": v(13.93, 0.6) * mm, "end": v(13.95, 0.54) * mm});
            skLineSegment(sketch, "E453", {"start": v(13.95, 0.54) * mm, "end": v(13.97, 0.48) * mm});
            skLineSegment(sketch, "E454", {"start": v(13.97, 0.48) * mm, "end": v(13.98, 0.43) * mm});
            skLineSegment(sketch, "E455", {"start": v(13.98, 0.43) * mm, "end": v(13.99, 0.32) * mm});
            skLineSegment(sketch, "E456", {"start": v(13.99, 0.32) * mm, "end": v(14, 0.09) * mm});
            skLineSegment(sketch, "E457", {"start": v(14, 0.09) * mm, "end": v(14.02, -0.09) * mm});
            skLineSegment(sketch, "E458", {"start": v(14.02, -0.09) * mm, "end": v(14.02, -0.2) * mm});
            skLineSegment(sketch, "E459", {"start": v(14.02, -0.2) * mm, "end": v(14.02, -0.27) * mm});
            skLineSegment(sketch, "E460", {"start": v(14.02, -0.27) * mm, "end": v(14.02, -0.33) * mm});
            skLineSegment(sketch, "E461", {"start": v(14.02, -0.33) * mm, "end": v(14.02, -0.39) * mm});
            skLineSegment(sketch, "E462", {"start": v(14.02, -0.39) * mm, "end": v(14, -0.45) * mm});
            skLineSegment(sketch, "E463", {"start": v(14, -0.45) * mm, "end": v(14, -0.5) * mm});
            skLineSegment(sketch, "E464", {"start": v(14, -0.5) * mm, "end": v(14, -0.56) * mm});
            skLineSegment(sketch, "E465", {"start": v(14, -0.56) * mm, "end": v(13.98, -0.62) * mm});
            skLineSegment(sketch, "E466", {"start": v(13.98, -0.62) * mm, "end": v(13.96, -0.67) * mm});
            skLineSegment(sketch, "E467", {"start": v(13.96, -0.67) * mm, "end": v(13.94, -0.73) * mm});
            skLineSegment(sketch, "E468", {"start": v(13.94, -0.73) * mm, "end": v(13.92, -0.78) * mm});
            skLineSegment(sketch, "E469", {"start": v(13.92, -0.78) * mm, "end": v(13.9, -0.83) * mm});
            skLineSegment(sketch, "E470", {"start": v(13.9, -0.83) * mm, "end": v(13.87, -0.88) * mm});
            skLineSegment(sketch, "E471", {"start": v(13.87, -0.88) * mm, "end": v(13.84, -0.93) * mm});
            skLineSegment(sketch, "E472", {"start": v(13.84, -0.93) * mm, "end": v(13.8, -0.97) * mm});
            skLineSegment(sketch, "E473", {"start": v(13.8, -0.97) * mm, "end": v(13.77, -1.02) * mm});
            skLineSegment(sketch, "E474", {"start": v(13.77, -1.02) * mm, "end": v(13.73, -1.06) * mm});
            skLineSegment(sketch, "E475", {"start": v(13.73, -1.06) * mm, "end": v(13.68, -1.1) * mm});
            skLineSegment(sketch, "E476", {"start": v(13.68, -1.1) * mm, "end": v(13.63, -1.14) * mm});
            skLineSegment(sketch, "E477", {"start": v(13.63, -1.14) * mm, "end": v(12.14, -1.17) * mm});
            skLineSegment(sketch, "E478", {"start": v(12.14, -1.17) * mm, "end": v(12.14, 1) * mm});
            skLineSegment(sketch, "E479", {"start": v(-13.67, -2.29) * mm, "end": v(-13.52, -2.27) * mm});
            skLineSegment(sketch, "E480", {"start": v(-13.52, -2.27) * mm, "end": v(-13.25, -2.24) * mm});
            skLineSegment(sketch, "E481", {"start": v(-13.25, -2.24) * mm, "end": v(-12.15, -2.23) * mm});
            skLineSegment(sketch, "E482", {"start": v(-12.15, -2.23) * mm, "end": v(-12.17, -4.39) * mm});
            skLineSegment(sketch, "E483", {"start": v(-12.17, -4.39) * mm, "end": v(-13.19, -4.41) * mm});
            skLineSegment(sketch, "E484", {"start": v(-13.19, -4.41) * mm, "end": v(-13.38, -4.4) * mm});
            skLineSegment(sketch, "E485", {"start": v(-13.38, -4.4) * mm, "end": v(-13.52, -4.38) * mm});
            skLineSegment(sketch, "E486", {"start": v(-13.52, -4.38) * mm, "end": v(-13.57, -4.38) * mm});
            skLineSegment(sketch, "E487", {"start": v(-13.57, -4.38) * mm, "end": v(-13.61, -4.36) * mm});
            skLineSegment(sketch, "E488", {"start": v(-13.61, -4.36) * mm, "end": v(-13.65, -4.35) * mm});
            skLineSegment(sketch, "E489", {"start": v(-13.65, -4.35) * mm, "end": v(-13.69, -4.33) * mm});
            skLineSegment(sketch, "E490", {"start": v(-13.69, -4.33) * mm, "end": v(-13.72, -4.3) * mm});
            skLineSegment(sketch, "E491", {"start": v(-13.72, -4.3) * mm, "end": v(-13.75, -4.28) * mm});
            skLineSegment(sketch, "E492", {"start": v(-13.75, -4.28) * mm, "end": v(-13.78, -4.26) * mm});
            skLineSegment(sketch, "E493", {"start": v(-13.78, -4.26) * mm, "end": v(-13.8, -4.23) * mm});
            skLineSegment(sketch, "E494", {"start": v(-13.8, -4.23) * mm, "end": v(-13.83, -4.2) * mm});
            skLineSegment(sketch, "E495", {"start": v(-13.83, -4.2) * mm, "end": v(-13.85, -4.17) * mm});
            skLineSegment(sketch, "E496", {"start": v(-13.85, -4.17) * mm, "end": v(-13.87, -4.13) * mm});
            skLineSegment(sketch, "E497", {"start": v(-13.87, -4.13) * mm, "end": v(-13.9, -4.1) * mm});
            skLineSegment(sketch, "E498", {"start": v(-13.9, -4.1) * mm, "end": v(-13.9, -4.06) * mm});
            skLineSegment(sketch, "E499", {"start": v(-13.9, -4.06) * mm, "end": v(-13.93, -4.02) * mm});
            skLineSegment(sketch, "E500", {"start": v(-13.93, -4.02) * mm, "end": v(-13.94, -3.99) * mm});
            skLineSegment(sketch, "E501", {"start": v(-13.94, -3.99) * mm, "end": v(-13.95, -3.95) * mm});
            skLineSegment(sketch, "E502", {"start": v(-13.95, -3.95) * mm, "end": v(-13.96, -3.9) * mm});
            skLineSegment(sketch, "E503", {"start": v(-13.96, -3.9) * mm, "end": v(-13.98, -3.82) * mm});
            skLineSegment(sketch, "E504", {"start": v(-13.98, -3.82) * mm, "end": v(-14, -3.74) * mm});
            skLineSegment(sketch, "E505", {"start": v(-14, -3.74) * mm, "end": v(-14, -3.62) * mm});
            skLineSegment(sketch, "E506", {"start": v(-14, -3.62) * mm, "end": v(-14.02, -3.5) * mm});
            skLineSegment(sketch, "E507", {"start": v(-14.02, -3.5) * mm, "end": v(-14.02, -3.42) * mm});
            skLineSegment(sketch, "E508", {"start": v(-14.02, -3.42) * mm, "end": v(-14.02, -3.38) * mm});
            skLineSegment(sketch, "E509", {"start": v(-14.02, -3.38) * mm, "end": v(-14.02, -3.27) * mm});
            skLineSegment(sketch, "E510", {"start": v(-14.02, -3.27) * mm, "end": v(-14.01, -3.06) * mm});
            skLineSegment(sketch, "E511", {"start": v(-14.01, -3.06) * mm, "end": v(-14, -2.93) * mm});
            skLineSegment(sketch, "E512", {"start": v(-14, -2.93) * mm, "end": v(-13.99, -2.85) * mm});
            skLineSegment(sketch, "E513", {"start": v(-13.99, -2.85) * mm, "end": v(-13.97, -2.76) * mm});
            skLineSegment(sketch, "E514", {"start": v(-13.97, -2.76) * mm, "end": v(-13.96, -2.72) * mm});
            skLineSegment(sketch, "E515", {"start": v(-13.96, -2.72) * mm, "end": v(-13.95, -2.68) * mm});
            skLineSegment(sketch, "E516", {"start": v(-13.95, -2.68) * mm, "end": v(-13.94, -2.64) * mm});
            skLineSegment(sketch, "E517", {"start": v(-13.94, -2.64) * mm, "end": v(-13.92, -2.6) * mm});
            skLineSegment(sketch, "E518", {"start": v(-13.92, -2.6) * mm, "end": v(-13.9, -2.57) * mm});
            skLineSegment(sketch, "E519", {"start": v(-13.9, -2.57) * mm, "end": v(-13.9, -2.53) * mm});
            skLineSegment(sketch, "E520", {"start": v(-13.9, -2.53) * mm, "end": v(-13.87, -2.5) * mm});
            skLineSegment(sketch, "E521", {"start": v(-13.87, -2.5) * mm, "end": v(-13.85, -2.46) * mm});
            skLineSegment(sketch, "E522", {"start": v(-13.85, -2.46) * mm, "end": v(-13.82, -2.43) * mm});
            skLineSegment(sketch, "E523", {"start": v(-13.82, -2.43) * mm, "end": v(-13.8, -2.4) * mm});
            skLineSegment(sketch, "E524", {"start": v(-13.8, -2.4) * mm, "end": v(-13.77, -2.37) * mm});
            skLineSegment(sketch, "E525", {"start": v(-13.77, -2.37) * mm, "end": v(-13.74, -2.34) * mm});
            skLineSegment(sketch, "E526", {"start": v(-13.74, -2.34) * mm, "end": v(-13.7, -2.31) * mm});
            skLineSegment(sketch, "E527", {"start": v(-13.7, -2.31) * mm, "end": v(-13.67, -2.29) * mm});
            skLineSegment(sketch, "E528", {"start": v(12.14, -2.23) * mm, "end": v(13.8, -2.28) * mm});
            skLineSegment(sketch, "E529", {"start": v(13.8, -2.28) * mm, "end": v(13.84, -2.4) * mm});
            skLineSegment(sketch, "E530", {"start": v(13.84, -2.4) * mm, "end": v(13.87, -2.5) * mm});
            skLineSegment(sketch, "E531", {"start": v(13.87, -2.5) * mm, "end": v(13.9, -2.6) * mm});
            skLineSegment(sketch, "E532", {"start": v(13.9, -2.6) * mm, "end": v(13.94, -2.72) * mm});
            skLineSegment(sketch, "E533", {"start": v(13.94, -2.72) * mm, "end": v(13.96, -2.83) * mm});
            skLineSegment(sketch, "E534", {"start": v(13.96, -2.83) * mm, "end": v(13.98, -2.95) * mm});
            skLineSegment(sketch, "E535", {"start": v(13.98, -2.95) * mm, "end": v(14, -3.06) * mm});
            skLineSegment(sketch, "E536", {"start": v(14, -3.06) * mm, "end": v(14.01, -3.18) * mm});
            skLineSegment(sketch, "E537", {"start": v(14.01, -3.18) * mm, "end": v(14.02, -3.3) * mm});
            skLineSegment(sketch, "E538", {"start": v(14.02, -3.3) * mm, "end": v(14.02, -3.35) * mm});
            skLineSegment(sketch, "E539", {"start": v(14.02, -3.35) * mm, "end": v(14.02, -3.4) * mm});
            skLineSegment(sketch, "E540", {"start": v(14.02, -3.4) * mm, "end": v(14.01, -3.47) * mm});
            skLineSegment(sketch, "E541", {"start": v(14.01, -3.47) * mm, "end": v(14.01, -3.52) * mm});
            skLineSegment(sketch, "E542", {"start": v(14.01, -3.52) * mm, "end": v(14, -3.58) * mm});
            skLineSegment(sketch, "E543", {"start": v(14, -3.58) * mm, "end": v(14, -3.64) * mm});
            skLineSegment(sketch, "E544", {"start": v(14, -3.64) * mm, "end": v(14, -3.7) * mm});
            skLineSegment(sketch, "E545", {"start": v(14, -3.7) * mm, "end": v(13.98, -3.75) * mm});
            skLineSegment(sketch, "E546", {"start": v(13.98, -3.75) * mm, "end": v(13.97, -3.81) * mm});
            skLineSegment(sketch, "E547", {"start": v(13.97, -3.81) * mm, "end": v(13.96, -3.87) * mm});
            skLineSegment(sketch, "E548", {"start": v(13.96, -3.87) * mm, "end": v(13.95, -3.92) * mm});
            skLineSegment(sketch, "E549", {"start": v(13.95, -3.92) * mm, "end": v(13.93, -4) * mm});
            skLineSegment(sketch, "E550", {"start": v(13.93, -4) * mm, "end": v(13.9, -4.09) * mm});
            skLineSegment(sketch, "E551", {"start": v(13.9, -4.09) * mm, "end": v(13.85, -4.16) * mm});
            skLineSegment(sketch, "E552", {"start": v(13.85, -4.16) * mm, "end": v(13.81, -4.22) * mm});
            skLineSegment(sketch, "E553", {"start": v(13.81, -4.22) * mm, "end": v(13.77, -4.26) * mm});
            skLineSegment(sketch, "E554", {"start": v(13.77, -4.26) * mm, "end": v(13.74, -4.3) * mm});
            skLineSegment(sketch, "E555", {"start": v(13.74, -4.3) * mm, "end": v(13.7, -4.32) * mm});
            skLineSegment(sketch, "E556", {"start": v(13.7, -4.32) * mm, "end": v(13.66, -4.34) * mm});
            skLineSegment(sketch, "E557", {"start": v(13.66, -4.34) * mm, "end": v(13.62, -4.35) * mm});
            skLineSegment(sketch, "E558", {"start": v(13.62, -4.35) * mm, "end": v(13.58, -4.37) * mm});
            skLineSegment(sketch, "E559", {"start": v(13.58, -4.37) * mm, "end": v(13.56, -4.37) * mm});
            skLineSegment(sketch, "E560", {"start": v(13.56, -4.37) * mm, "end": v(12.16, -4.4) * mm});
            skLineSegment(sketch, "E561", {"start": v(12.16, -4.4) * mm, "end": v(12.14, -2.23) * mm});
            skLineSegment(sketch, "E562", {"start": v(-13.8, -5.52) * mm, "end": v(-12.15, -5.47) * mm});
            skLineSegment(sketch, "E563", {"start": v(-12.15, -5.47) * mm, "end": v(-12.17, -7.63) * mm});
            skLineSegment(sketch, "E564", {"start": v(-12.17, -7.63) * mm, "end": v(-12.23, -7.62) * mm});
            skLineSegment(sketch, "E565", {"start": v(-12.23, -7.62) * mm, "end": v(-12.29, -7.62) * mm});
            skLineSegment(sketch, "E566", {"start": v(-12.29, -7.62) * mm, "end": v(-12.35, -7.61) * mm});
            skLineSegment(sketch, "E567", {"start": v(-12.35, -7.61) * mm, "end": v(-12.4, -7.61) * mm});
            skLineSegment(sketch, "E568", {"start": v(-12.4, -7.61) * mm, "end": v(-12.47, -7.62) * mm});
            skLineSegment(sketch, "E569", {"start": v(-12.47, -7.62) * mm, "end": v(-12.6, -7.63) * mm});
            skLineSegment(sketch, "E570", {"start": v(-12.6, -7.63) * mm, "end": v(-12.98, -7.66) * mm});
            skLineSegment(sketch, "E571", {"start": v(-12.98, -7.66) * mm, "end": v(-13.05, -7.67) * mm});
            skLineSegment(sketch, "E572", {"start": v(-13.05, -7.67) * mm, "end": v(-13.1, -7.67) * mm});
            skLineSegment(sketch, "E573", {"start": v(-13.1, -7.67) * mm, "end": v(-13.17, -7.67) * mm});
            skLineSegment(sketch, "E574", {"start": v(-13.17, -7.67) * mm, "end": v(-13.24, -7.67) * mm});
            skLineSegment(sketch, "E575", {"start": v(-13.24, -7.67) * mm, "end": v(-13.3, -7.67) * mm});
            skLineSegment(sketch, "E576", {"start": v(-13.3, -7.67) * mm, "end": v(-13.36, -7.66) * mm});
            skLineSegment(sketch, "E577", {"start": v(-13.36, -7.66) * mm, "end": v(-13.42, -7.65) * mm});
            skLineSegment(sketch, "E578", {"start": v(-13.42, -7.65) * mm, "end": v(-13.48, -7.64) * mm});
            skLineSegment(sketch, "E579", {"start": v(-13.48, -7.64) * mm, "end": v(-13.53, -7.63) * mm});
            skLineSegment(sketch, "E580", {"start": v(-13.53, -7.63) * mm, "end": v(-13.59, -7.6) * mm});
            skLineSegment(sketch, "E581", {"start": v(-13.59, -7.6) * mm, "end": v(-13.64, -7.58) * mm});
            skLineSegment(sketch, "E582", {"start": v(-13.64, -7.58) * mm, "end": v(-13.7, -7.55) * mm});
            skLineSegment(sketch, "E583", {"start": v(-13.7, -7.55) * mm, "end": v(-13.74, -7.52) * mm});
            skLineSegment(sketch, "E584", {"start": v(-13.74, -7.52) * mm, "end": v(-13.8, -7.48) * mm});
            skLineSegment(sketch, "E585", {"start": v(-13.8, -7.48) * mm, "end": v(-13.84, -7.44) * mm});
            skLineSegment(sketch, "E586", {"start": v(-13.84, -7.44) * mm, "end": v(-13.88, -7.39) * mm});
            skLineSegment(sketch, "E587", {"start": v(-13.88, -7.39) * mm, "end": v(-13.9, -7.33) * mm});
            skLineSegment(sketch, "E588", {"start": v(-13.9, -7.33) * mm, "end": v(-13.92, -7.26) * mm});
            skLineSegment(sketch, "E589", {"start": v(-13.92, -7.26) * mm, "end": v(-13.94, -7.2) * mm});
            skLineSegment(sketch, "E590", {"start": v(-13.94, -7.2) * mm, "end": v(-13.96, -7.14) * mm});
            skLineSegment(sketch, "E591", {"start": v(-13.96, -7.14) * mm, "end": v(-13.97, -7.07) * mm});
            skLineSegment(sketch, "E592", {"start": v(-13.97, -7.07) * mm, "end": v(-13.99, -7) * mm});
            skLineSegment(sketch, "E593", {"start": v(-13.99, -7) * mm, "end": v(-14, -6.94) * mm});
            skLineSegment(sketch, "E594", {"start": v(-14, -6.94) * mm, "end": v(-14, -6.88) * mm});
            skLineSegment(sketch, "E595", {"start": v(-14, -6.88) * mm, "end": v(-14.01, -6.81) * mm});
            skLineSegment(sketch, "E596", {"start": v(-14.01, -6.81) * mm, "end": v(-14.02, -6.75) * mm});
            skLineSegment(sketch, "E597", {"start": v(-14.02, -6.75) * mm, "end": v(-14.02, -6.68) * mm});
            skLineSegment(sketch, "E598", {"start": v(-14.02, -6.68) * mm, "end": v(-14.02, -6.62) * mm});
            skLineSegment(sketch, "E599", {"start": v(-14.02, -6.62) * mm, "end": v(-14.02, -6.55) * mm});
            skLineSegment(sketch, "E600", {"start": v(-14.02, -6.55) * mm, "end": v(-14.02, -6.48) * mm});
            skLineSegment(sketch, "E601", {"start": v(-14.02, -6.48) * mm, "end": v(-14.02, -6.42) * mm});
            skLineSegment(sketch, "E602", {"start": v(-14.02, -6.42) * mm, "end": v(-14.01, -6.35) * mm});
            skLineSegment(sketch, "E603", {"start": v(-14.01, -6.35) * mm, "end": v(-14, -6.29) * mm});
            skLineSegment(sketch, "E604", {"start": v(-14, -6.29) * mm, "end": v(-14, -6.22) * mm});
            skLineSegment(sketch, "E605", {"start": v(-14, -6.22) * mm, "end": v(-13.99, -6.15) * mm});
            skLineSegment(sketch, "E606", {"start": v(-13.99, -6.15) * mm, "end": v(-13.97, -6.09) * mm});
            skLineSegment(sketch, "E607", {"start": v(-13.97, -6.09) * mm, "end": v(-13.96, -6.03) * mm});
            skLineSegment(sketch, "E608", {"start": v(-13.96, -6.03) * mm, "end": v(-13.95, -5.96) * mm});
            skLineSegment(sketch, "E609", {"start": v(-13.95, -5.96) * mm, "end": v(-13.93, -5.9) * mm});
            skLineSegment(sketch, "E610", {"start": v(-13.93, -5.9) * mm, "end": v(-13.91, -5.83) * mm});
            skLineSegment(sketch, "E611", {"start": v(-13.91, -5.83) * mm, "end": v(-13.9, -5.77) * mm});
            skLineSegment(sketch, "E612", {"start": v(-13.9, -5.77) * mm, "end": v(-13.87, -5.7) * mm});
            skLineSegment(sketch, "E613", {"start": v(-13.87, -5.7) * mm, "end": v(-13.85, -5.65) * mm});
            skLineSegment(sketch, "E614", {"start": v(-13.85, -5.65) * mm, "end": v(-13.82, -5.58) * mm});
            skLineSegment(sketch, "E615", {"start": v(-13.82, -5.58) * mm, "end": v(-13.8, -5.52) * mm});
            skLineSegment(sketch, "E616", {"start": v(12.14, -5.47) * mm, "end": v(13.8, -5.52) * mm});
            skLineSegment(sketch, "E617", {"start": v(13.8, -5.52) * mm, "end": v(13.82, -5.59) * mm});
            skLineSegment(sketch, "E618", {"start": v(13.82, -5.59) * mm, "end": v(13.84, -5.66) * mm});
            skLineSegment(sketch, "E619", {"start": v(13.84, -5.66) * mm, "end": v(13.87, -5.73) * mm});
            skLineSegment(sketch, "E620", {"start": v(13.87, -5.73) * mm, "end": v(13.89, -5.8) * mm});
            skLineSegment(sketch, "E621", {"start": v(13.89, -5.8) * mm, "end": v(13.91, -5.87) * mm});
            skLineSegment(sketch, "E622", {"start": v(13.91, -5.87) * mm, "end": v(13.93, -5.94) * mm});
            skLineSegment(sketch, "E623", {"start": v(13.93, -5.94) * mm, "end": v(13.95, -6.02) * mm});
            skLineSegment(sketch, "E624", {"start": v(13.95, -6.02) * mm, "end": v(13.97, -6.1) * mm});
            skLineSegment(sketch, "E625", {"start": v(13.97, -6.1) * mm, "end": v(13.98, -6.17) * mm});
            skLineSegment(sketch, "E626", {"start": v(13.98, -6.17) * mm, "end": v(14, -6.24) * mm});
            skLineSegment(sketch, "E627", {"start": v(14, -6.24) * mm, "end": v(14, -6.32) * mm});
            skLineSegment(sketch, "E628", {"start": v(14, -6.32) * mm, "end": v(14.02, -6.4) * mm});
            skLineSegment(sketch, "E629", {"start": v(14.02, -6.4) * mm, "end": v(14.02, -6.47) * mm});
            skLineSegment(sketch, "E630", {"start": v(14.02, -6.47) * mm, "end": v(14.03, -6.55) * mm});
            skLineSegment(sketch, "E631", {"start": v(14.03, -6.55) * mm, "end": v(14.03, -6.62) * mm});
            skLineSegment(sketch, "E632", {"start": v(14.03, -6.62) * mm, "end": v(14.03, -6.7) * mm});
            skLineSegment(sketch, "E633", {"start": v(14.03, -6.7) * mm, "end": v(14.02, -6.77) * mm});
            skLineSegment(sketch, "E634", {"start": v(14.02, -6.77) * mm, "end": v(14.02, -6.85) * mm});
            skLineSegment(sketch, "E635", {"start": v(14.02, -6.85) * mm, "end": v(14, -6.92) * mm});
            skLineSegment(sketch, "E636", {"start": v(14, -6.92) * mm, "end": v(14, -7) * mm});
            skLineSegment(sketch, "E637", {"start": v(14, -7) * mm, "end": v(13.98, -7.06) * mm});
            skLineSegment(sketch, "E638", {"start": v(13.98, -7.06) * mm, "end": v(13.96, -7.13) * mm});
            skLineSegment(sketch, "E639", {"start": v(13.96, -7.13) * mm, "end": v(13.93, -7.2) * mm});
            skLineSegment(sketch, "E640", {"start": v(13.93, -7.2) * mm, "end": v(13.9, -7.27) * mm});
            skLineSegment(sketch, "E641", {"start": v(13.9, -7.27) * mm, "end": v(13.87, -7.33) * mm});
            skLineSegment(sketch, "E642", {"start": v(13.87, -7.33) * mm, "end": v(13.83, -7.4) * mm});
            skLineSegment(sketch, "E643", {"start": v(13.83, -7.4) * mm, "end": v(13.8, -7.45) * mm});
            skLineSegment(sketch, "E644", {"start": v(13.8, -7.45) * mm, "end": v(13.75, -7.51) * mm});
            skLineSegment(sketch, "E645", {"start": v(13.75, -7.51) * mm, "end": v(13.7, -7.57) * mm});
            skLineSegment(sketch, "E646", {"start": v(13.7, -7.57) * mm, "end": v(13.65, -7.58) * mm});
            skLineSegment(sketch, "E647", {"start": v(13.65, -7.58) * mm, "end": v(13.6, -7.6) * mm});
            skLineSegment(sketch, "E648", {"start": v(13.6, -7.6) * mm, "end": v(13.54, -7.6) * mm});
            skLineSegment(sketch, "E649", {"start": v(13.54, -7.6) * mm, "end": v(13.5, -7.62) * mm});
            skLineSegment(sketch, "E650", {"start": v(13.5, -7.62) * mm, "end": v(13.44, -7.63) * mm});
            skLineSegment(sketch, "E651", {"start": v(13.44, -7.63) * mm, "end": v(13.34, -7.64) * mm});
            skLineSegment(sketch, "E652", {"start": v(13.34, -7.64) * mm, "end": v(13.23, -7.65) * mm});
            skLineSegment(sketch, "E653", {"start": v(13.23, -7.65) * mm, "end": v(13.07, -7.65) * mm});
            skLineSegment(sketch, "E654", {"start": v(13.07, -7.65) * mm, "end": v(12.32, -7.63) * mm});
            skLineSegment(sketch, "E655", {"start": v(12.32, -7.63) * mm, "end": v(12.16, -7.63) * mm});
            skLineSegment(sketch, "E656", {"start": v(12.16, -7.63) * mm, "end": v(12.14, -5.47) * mm});
            skLineSegment(sketch, "E657", {"start": v(-5.9, -10.04) * mm, "end": v(-3.75, -10.04) * mm});
            skLineSegment(sketch, "E658", {"start": v(-3.75, -10.04) * mm, "end": v(-3.75, -11.23) * mm});
            skLineSegment(sketch, "E659", {"start": v(-3.75, -11.23) * mm, "end": v(-3.77, -11.42) * mm});
            skLineSegment(sketch, "E660", {"start": v(-3.77, -11.42) * mm, "end": v(-3.77, -11.44) * mm});
            skLineSegment(sketch, "E661", {"start": v(-3.77, -11.44) * mm, "end": v(-3.78, -11.47) * mm});
            skLineSegment(sketch, "E662", {"start": v(-3.78, -11.47) * mm, "end": v(-3.78, -11.5) * mm});
            skLineSegment(sketch, "E663", {"start": v(-3.78, -11.5) * mm, "end": v(-3.8, -11.51) * mm});
            skLineSegment(sketch, "E664", {"start": v(-3.8, -11.51) * mm, "end": v(-3.8, -11.54) * mm});
            skLineSegment(sketch, "E665", {"start": v(-3.8, -11.54) * mm, "end": v(-3.82, -11.56) * mm});
            skLineSegment(sketch, "E666", {"start": v(-3.82, -11.56) * mm, "end": v(-3.83, -11.58) * mm});
            skLineSegment(sketch, "E667", {"start": v(-3.83, -11.58) * mm, "end": v(-3.84, -11.6) * mm});
            skLineSegment(sketch, "E668", {"start": v(-3.84, -11.6) * mm, "end": v(-3.86, -11.61) * mm});
            skLineSegment(sketch, "E669", {"start": v(-3.86, -11.61) * mm, "end": v(-3.9, -11.65) * mm});
            skLineSegment(sketch, "E670", {"start": v(-3.9, -11.65) * mm, "end": v(-3.93, -11.68) * mm});
            skLineSegment(sketch, "E671", {"start": v(-3.93, -11.68) * mm, "end": v(-4, -11.72) * mm});
            skLineSegment(sketch, "E672", {"start": v(-4, -11.72) * mm, "end": v(-4.1, -11.78) * mm});
            skLineSegment(sketch, "E673", {"start": v(-4.1, -11.78) * mm, "end": v(-4.3, -11.85) * mm});
            skLineSegment(sketch, "E674", {"start": v(-4.3, -11.85) * mm, "end": v(-4.4, -11.87) * mm});
            skLineSegment(sketch, "E675", {"start": v(-4.4, -11.87) * mm, "end": v(-4.46, -11.88) * mm});
            skLineSegment(sketch, "E676", {"start": v(-4.46, -11.88) * mm, "end": v(-4.52, -11.89) * mm});
            skLineSegment(sketch, "E677", {"start": v(-4.52, -11.89) * mm, "end": v(-4.58, -11.9) * mm});
            skLineSegment(sketch, "E678", {"start": v(-4.58, -11.9) * mm, "end": v(-4.64, -11.9) * mm});
            skLineSegment(sketch, "E679", {"start": v(-4.64, -11.9) * mm, "end": v(-4.7, -11.9) * mm});
            skLineSegment(sketch, "E680", {"start": v(-4.7, -11.9) * mm, "end": v(-4.76, -11.9) * mm});
            skLineSegment(sketch, "E681", {"start": v(-4.76, -11.9) * mm, "end": v(-4.82, -11.9) * mm});
            skLineSegment(sketch, "E682", {"start": v(-4.82, -11.9) * mm, "end": v(-4.88, -11.9) * mm});
            skLineSegment(sketch, "E683", {"start": v(-4.88, -11.9) * mm, "end": v(-4.94, -11.9) * mm});
            skLineSegment(sketch, "E684", {"start": v(-4.94, -11.9) * mm, "end": v(-5, -11.9) * mm});
            skLineSegment(sketch, "E685", {"start": v(-5, -11.9) * mm, "end": v(-5.05, -11.9) * mm});
            skLineSegment(sketch, "E686", {"start": v(-5.05, -11.9) * mm, "end": v(-5.11, -11.9) * mm});
            skLineSegment(sketch, "E687", {"start": v(-5.11, -11.9) * mm, "end": v(-5.17, -11.89) * mm});
            skLineSegment(sketch, "E688", {"start": v(-5.17, -11.89) * mm, "end": v(-5.23, -11.88) * mm});
            skLineSegment(sketch, "E689", {"start": v(-5.23, -11.88) * mm, "end": v(-5.29, -11.86) * mm});
            skLineSegment(sketch, "E690", {"start": v(-5.29, -11.86) * mm, "end": v(-5.34, -11.85) * mm});
            skLineSegment(sketch, "E691", {"start": v(-5.34, -11.85) * mm, "end": v(-5.4, -11.84) * mm});
            skLineSegment(sketch, "E692", {"start": v(-5.4, -11.84) * mm, "end": v(-5.46, -11.82) * mm});
            skLineSegment(sketch, "E693", {"start": v(-5.46, -11.82) * mm, "end": v(-5.51, -11.8) * mm});
            skLineSegment(sketch, "E694", {"start": v(-5.51, -11.8) * mm, "end": v(-5.57, -11.78) * mm});
            skLineSegment(sketch, "E695", {"start": v(-5.57, -11.78) * mm, "end": v(-5.62, -11.75) * mm});
            skLineSegment(sketch, "E696", {"start": v(-5.62, -11.75) * mm, "end": v(-5.67, -11.73) * mm});
            skLineSegment(sketch, "E697", {"start": v(-5.67, -11.73) * mm, "end": v(-5.72, -11.7) * mm});
            skLineSegment(sketch, "E698", {"start": v(-5.72, -11.7) * mm, "end": v(-5.78, -11.67) * mm});
            skLineSegment(sketch, "E699", {"start": v(-5.78, -11.67) * mm, "end": v(-5.83, -11.64) * mm});
            skLineSegment(sketch, "E700", {"start": v(-5.83, -11.64) * mm, "end": v(-5.88, -11.6) * mm});
            skLineSegment(sketch, "E701", {"start": v(-5.88, -11.6) * mm, "end": v(-5.92, -11.57) * mm});
            skLineSegment(sketch, "E702", {"start": v(-5.92, -11.57) * mm, "end": v(-5.9, -10.04) * mm});
            skLineSegment(sketch, "E703", {"start": v(-2.74, -10.04) * mm, "end": v(-0.56, -10.04) * mm});
            skLineSegment(sketch, "E704", {"start": v(-0.56, -10.04) * mm, "end": v(-0.53, -11.25) * mm});
            skLineSegment(sketch, "E705", {"start": v(-0.53, -11.25) * mm, "end": v(-0.54, -11.34) * mm});
            skLineSegment(sketch, "E706", {"start": v(-0.54, -11.34) * mm, "end": v(-0.56, -11.42) * mm});
            skLineSegment(sketch, "E707", {"start": v(-0.56, -11.42) * mm, "end": v(-0.6, -11.49) * mm});
            skLineSegment(sketch, "E708", {"start": v(-0.6, -11.49) * mm, "end": v(-0.63, -11.56) * mm});
            skLineSegment(sketch, "E709", {"start": v(-0.63, -11.56) * mm, "end": v(-0.68, -11.62) * mm});
            skLineSegment(sketch, "E710", {"start": v(-0.68, -11.62) * mm, "end": v(-0.7, -11.67) * mm});
            skLineSegment(sketch, "E711", {"start": v(-0.7, -11.67) * mm, "end": v(-0.75, -11.7) * mm});
            skLineSegment(sketch, "E712", {"start": v(-0.75, -11.7) * mm, "end": v(-0.79, -11.74) * mm});
            skLineSegment(sketch, "E713", {"start": v(-0.79, -11.74) * mm, "end": v(-0.83, -11.77) * mm});
            skLineSegment(sketch, "E714", {"start": v(-0.83, -11.77) * mm, "end": v(-0.87, -11.8) * mm});
            skLineSegment(sketch, "E715", {"start": v(-0.87, -11.8) * mm, "end": v(-0.9, -11.8) * mm});
            skLineSegment(sketch, "E716", {"start": v(-0.9, -11.8) * mm, "end": v(-0.92, -11.81) * mm});
            skLineSegment(sketch, "E717", {"start": v(-0.92, -11.81) * mm, "end": v(-0.95, -11.82) * mm});
            skLineSegment(sketch, "E718", {"start": v(-0.95, -11.82) * mm, "end": v(-0.97, -11.83) * mm});
            skLineSegment(sketch, "E719", {"start": v(-0.97, -11.83) * mm, "end": v(-1, -11.84) * mm});
            skLineSegment(sketch, "E720", {"start": v(-1, -11.84) * mm, "end": v(-1.02, -11.84) * mm});
            skLineSegment(sketch, "E721", {"start": v(-1.02, -11.84) * mm, "end": v(-1.05, -11.84) * mm});
            skLineSegment(sketch, "E722", {"start": v(-1.05, -11.84) * mm, "end": v(-1.1, -11.85) * mm});
            skLineSegment(sketch, "E723", {"start": v(-1.1, -11.85) * mm, "end": v(-1.22, -11.88) * mm});
            skLineSegment(sketch, "E724", {"start": v(-1.22, -11.88) * mm, "end": v(-1.34, -11.9) * mm});
            skLineSegment(sketch, "E725", {"start": v(-1.34, -11.9) * mm, "end": v(-1.47, -11.9) * mm});
            skLineSegment(sketch, "E726", {"start": v(-1.47, -11.9) * mm, "end": v(-1.53, -11.91) * mm});
            skLineSegment(sketch, "E727", {"start": v(-1.53, -11.91) * mm, "end": v(-1.59, -11.91) * mm});
            skLineSegment(sketch, "E728", {"start": v(-1.59, -11.91) * mm, "end": v(-1.65, -11.92) * mm});
            skLineSegment(sketch, "E729", {"start": v(-1.65, -11.92) * mm, "end": v(-1.71, -11.92) * mm});
            skLineSegment(sketch, "E730", {"start": v(-1.71, -11.92) * mm, "end": v(-1.78, -11.91) * mm});
            skLineSegment(sketch, "E731", {"start": v(-1.78, -11.91) * mm, "end": v(-1.84, -11.9) * mm});
            skLineSegment(sketch, "E732", {"start": v(-1.84, -11.9) * mm, "end": v(-1.9, -11.9) * mm});
            skLineSegment(sketch, "E733", {"start": v(-1.9, -11.9) * mm, "end": v(-1.96, -11.9) * mm});
            skLineSegment(sketch, "E734", {"start": v(-1.96, -11.9) * mm, "end": v(-2.02, -11.89) * mm});
            skLineSegment(sketch, "E735", {"start": v(-2.02, -11.89) * mm, "end": v(-2.08, -11.87) * mm});
            skLineSegment(sketch, "E736", {"start": v(-2.08, -11.87) * mm, "end": v(-2.14, -11.86) * mm});
            skLineSegment(sketch, "E737", {"start": v(-2.14, -11.86) * mm, "end": v(-2.2, -11.84) * mm});
            skLineSegment(sketch, "E738", {"start": v(-2.2, -11.84) * mm, "end": v(-2.25, -11.82) * mm});
            skLineSegment(sketch, "E739", {"start": v(-2.25, -11.82) * mm, "end": v(-2.3, -11.8) * mm});
            skLineSegment(sketch, "E740", {"start": v(-2.3, -11.8) * mm, "end": v(-2.36, -11.77) * mm});
            skLineSegment(sketch, "E741", {"start": v(-2.36, -11.77) * mm, "end": v(-2.41, -11.74) * mm});
            skLineSegment(sketch, "E742", {"start": v(-2.41, -11.74) * mm, "end": v(-2.46, -11.7) * mm});
            skLineSegment(sketch, "E743", {"start": v(-2.46, -11.7) * mm, "end": v(-2.5, -11.67) * mm});
            skLineSegment(sketch, "E744", {"start": v(-2.5, -11.67) * mm, "end": v(-2.55, -11.63) * mm});
            skLineSegment(sketch, "E745", {"start": v(-2.55, -11.63) * mm, "end": v(-2.6, -11.58) * mm});
            skLineSegment(sketch, "E746", {"start": v(-2.6, -11.58) * mm, "end": v(-2.64, -11.54) * mm});
            skLineSegment(sketch, "E747", {"start": v(-2.64, -11.54) * mm, "end": v(-2.68, -11.49) * mm});
            skLineSegment(sketch, "E748", {"start": v(-2.68, -11.49) * mm, "end": v(-2.7, -11.39) * mm});
            skLineSegment(sketch, "E749", {"start": v(-2.7, -11.39) * mm, "end": v(-2.71, -11.24) * mm});
            skLineSegment(sketch, "E750", {"start": v(-2.71, -11.24) * mm, "end": v(-2.73, -11) * mm});
            skLineSegment(sketch, "E751", {"start": v(-2.73, -11) * mm, "end": v(-2.74, -10.04) * mm});
            skLineSegment(sketch, "E752", {"start": v(0.56, -10.04) * mm, "end": v(2.73, -10.04) * mm});
            skLineSegment(sketch, "E753", {"start": v(2.73, -10.04) * mm, "end": v(2.74, -11.03) * mm});
            skLineSegment(sketch, "E754", {"start": v(2.74, -11.03) * mm, "end": v(2.72, -11.26) * mm});
            skLineSegment(sketch, "E755", {"start": v(2.72, -11.26) * mm, "end": v(2.7, -11.4) * mm});
            skLineSegment(sketch, "E756", {"start": v(2.7, -11.4) * mm, "end": v(2.68, -11.45) * mm});
            skLineSegment(sketch, "E757", {"start": v(2.68, -11.45) * mm, "end": v(2.66, -11.5) * mm});
            skLineSegment(sketch, "E758", {"start": v(2.66, -11.5) * mm, "end": v(2.63, -11.54) * mm});
            skLineSegment(sketch, "E759", {"start": v(2.63, -11.54) * mm, "end": v(2.6, -11.58) * mm});
            skLineSegment(sketch, "E760", {"start": v(2.6, -11.58) * mm, "end": v(2.57, -11.62) * mm});
            skLineSegment(sketch, "E761", {"start": v(2.57, -11.62) * mm, "end": v(2.54, -11.65) * mm});
            skLineSegment(sketch, "E762", {"start": v(2.54, -11.65) * mm, "end": v(2.5, -11.68) * mm});
            skLineSegment(sketch, "E763", {"start": v(2.5, -11.68) * mm, "end": v(2.46, -11.7) * mm});
            skLineSegment(sketch, "E764", {"start": v(2.46, -11.7) * mm, "end": v(2.42, -11.74) * mm});
            skLineSegment(sketch, "E765", {"start": v(2.42, -11.74) * mm, "end": v(2.38, -11.76) * mm});
            skLineSegment(sketch, "E766", {"start": v(2.38, -11.76) * mm, "end": v(2.34, -11.78) * mm});
            skLineSegment(sketch, "E767", {"start": v(2.34, -11.78) * mm, "end": v(2.3, -11.8) * mm});
            skLineSegment(sketch, "E768", {"start": v(2.3, -11.8) * mm, "end": v(2.25, -11.82) * mm});
            skLineSegment(sketch, "E769", {"start": v(2.25, -11.82) * mm, "end": v(2.2, -11.84) * mm});
            skLineSegment(sketch, "E770", {"start": v(2.2, -11.84) * mm, "end": v(2.15, -11.85) * mm});
            skLineSegment(sketch, "E771", {"start": v(2.15, -11.85) * mm, "end": v(2.1, -11.86) * mm});
            skLineSegment(sketch, "E772", {"start": v(2.1, -11.86) * mm, "end": v(2.06, -11.87) * mm});
            skLineSegment(sketch, "E773", {"start": v(2.06, -11.87) * mm, "end": v(2, -11.88) * mm});
            skLineSegment(sketch, "E774", {"start": v(2, -11.88) * mm, "end": v(1.96, -11.89) * mm});
            skLineSegment(sketch, "E775", {"start": v(1.96, -11.89) * mm, "end": v(1.86, -11.9) * mm});
            skLineSegment(sketch, "E776", {"start": v(1.86, -11.9) * mm, "end": v(1.76, -11.9) * mm});
            skLineSegment(sketch, "E777", {"start": v(1.76, -11.9) * mm, "end": v(1.66, -11.9) * mm});
            skLineSegment(sketch, "E778", {"start": v(1.66, -11.9) * mm, "end": v(1.56, -11.9) * mm});
            skLineSegment(sketch, "E779", {"start": v(1.56, -11.9) * mm, "end": v(1.47, -11.9) * mm});
            skLineSegment(sketch, "E780", {"start": v(1.47, -11.9) * mm, "end": v(1.4, -11.9) * mm});
            skLineSegment(sketch, "E781", {"start": v(1.4, -11.9) * mm, "end": v(1.32, -11.9) * mm});
            skLineSegment(sketch, "E782", {"start": v(1.32, -11.9) * mm, "end": v(1.24, -11.89) * mm});
            skLineSegment(sketch, "E783", {"start": v(1.24, -11.89) * mm, "end": v(1.17, -11.88) * mm});
            skLineSegment(sketch, "E784", {"start": v(1.17, -11.88) * mm, "end": v(1.1, -11.86) * mm});
            skLineSegment(sketch, "E785", {"start": v(1.1, -11.86) * mm, "end": v(1.06, -11.85) * mm});
            skLineSegment(sketch, "E786", {"start": v(1.06, -11.85) * mm, "end": v(1.02, -11.84) * mm});
            skLineSegment(sketch, "E787", {"start": v(1.02, -11.84) * mm, "end": v(0.98, -11.83) * mm});
            skLineSegment(sketch, "E788", {"start": v(0.98, -11.83) * mm, "end": v(0.95, -11.81) * mm});
            skLineSegment(sketch, "E789", {"start": v(0.95, -11.81) * mm, "end": v(0.91, -11.8) * mm});
            skLineSegment(sketch, "E790", {"start": v(0.91, -11.8) * mm, "end": v(0.88, -11.78) * mm});
            skLineSegment(sketch, "E791", {"start": v(0.88, -11.78) * mm, "end": v(0.85, -11.76) * mm});
            skLineSegment(sketch, "E792", {"start": v(0.85, -11.76) * mm, "end": v(0.81, -11.74) * mm});
            skLineSegment(sketch, "E793", {"start": v(0.81, -11.74) * mm, "end": v(0.78, -11.72) * mm});
            skLineSegment(sketch, "E794", {"start": v(0.78, -11.72) * mm, "end": v(0.75, -11.7) * mm});
            skLineSegment(sketch, "E795", {"start": v(0.75, -11.7) * mm, "end": v(0.72, -11.68) * mm});
            skLineSegment(sketch, "E796", {"start": v(0.72, -11.68) * mm, "end": v(0.7, -11.65) * mm});
            skLineSegment(sketch, "E797", {"start": v(0.7, -11.65) * mm, "end": v(0.67, -11.63) * mm});
            skLineSegment(sketch, "E798", {"start": v(0.67, -11.63) * mm, "end": v(0.65, -11.6) * mm});
            skLineSegment(sketch, "E799", {"start": v(0.65, -11.6) * mm, "end": v(0.63, -11.57) * mm});
            skLineSegment(sketch, "E800", {"start": v(0.63, -11.57) * mm, "end": v(0.6, -11.54) * mm});
            skLineSegment(sketch, "E801", {"start": v(0.6, -11.54) * mm, "end": v(0.59, -11.5) * mm});
            skLineSegment(sketch, "E802", {"start": v(0.59, -11.5) * mm, "end": v(0.57, -11.47) * mm});
            skLineSegment(sketch, "E803", {"start": v(0.57, -11.47) * mm, "end": v(0.55, -11.43) * mm});
            skLineSegment(sketch, "E804", {"start": v(0.55, -11.43) * mm, "end": v(0.53, -11.29) * mm});
            skLineSegment(sketch, "E805", {"start": v(0.53, -11.29) * mm, "end": v(0.52, -11.1) * mm});
            skLineSegment(sketch, "E806", {"start": v(0.52, -11.1) * mm, "end": v(0.52, -10.71) * mm});
            skLineSegment(sketch, "E807", {"start": v(0.52, -10.71) * mm, "end": v(0.56, -10.04) * mm});
            skLineSegment(sketch, "E808", {"start": v(3.74, -10.04) * mm, "end": v(5.9, -10.04) * mm});
            skLineSegment(sketch, "E809", {"start": v(5.9, -10.04) * mm, "end": v(5.92, -11.57) * mm});
            skLineSegment(sketch, "E810", {"start": v(5.92, -11.57) * mm, "end": v(5.87, -11.61) * mm});
            skLineSegment(sketch, "E811", {"start": v(5.87, -11.61) * mm, "end": v(5.82, -11.64) * mm});
            skLineSegment(sketch, "E812", {"start": v(5.82, -11.64) * mm, "end": v(5.77, -11.68) * mm});
            skLineSegment(sketch, "E813", {"start": v(5.77, -11.68) * mm, "end": v(5.71, -11.7) * mm});
            skLineSegment(sketch, "E814", {"start": v(5.71, -11.7) * mm, "end": v(5.66, -11.73) * mm});
            skLineSegment(sketch, "E815", {"start": v(5.66, -11.73) * mm, "end": v(5.6, -11.76) * mm});
            skLineSegment(sketch, "E816", {"start": v(5.6, -11.76) * mm, "end": v(5.55, -11.78) * mm});
            skLineSegment(sketch, "E817", {"start": v(5.55, -11.78) * mm, "end": v(5.5, -11.8) * mm});
            skLineSegment(sketch, "E818", {"start": v(5.5, -11.8) * mm, "end": v(5.43, -11.82) * mm});
            skLineSegment(sketch, "E819", {"start": v(5.43, -11.82) * mm, "end": v(5.38, -11.84) * mm});
            skLineSegment(sketch, "E820", {"start": v(5.38, -11.84) * mm, "end": v(5.32, -11.86) * mm});
            skLineSegment(sketch, "E821", {"start": v(5.32, -11.86) * mm, "end": v(5.26, -11.87) * mm});
            skLineSegment(sketch, "E822", {"start": v(5.26, -11.87) * mm, "end": v(5.2, -11.88) * mm});
            skLineSegment(sketch, "E823", {"start": v(5.2, -11.88) * mm, "end": v(5.14, -11.89) * mm});
            skLineSegment(sketch, "E824", {"start": v(5.14, -11.89) * mm, "end": v(5.08, -11.9) * mm});
            skLineSegment(sketch, "E825", {"start": v(5.08, -11.9) * mm, "end": v(5.02, -11.9) * mm});
            skLineSegment(sketch, "E826", {"start": v(5.02, -11.9) * mm, "end": v(4.96, -11.9) * mm});
            skLineSegment(sketch, "E827", {"start": v(4.96, -11.9) * mm, "end": v(4.9, -11.91) * mm});
            skLineSegment(sketch, "E828", {"start": v(4.9, -11.91) * mm, "end": v(4.84, -11.91) * mm});
            skLineSegment(sketch, "E829", {"start": v(4.84, -11.91) * mm, "end": v(4.78, -11.91) * mm});
            skLineSegment(sketch, "E830", {"start": v(4.78, -11.91) * mm, "end": v(4.72, -11.9) * mm});
            skLineSegment(sketch, "E831", {"start": v(4.72, -11.9) * mm, "end": v(4.65, -11.9) * mm});
            skLineSegment(sketch, "E832", {"start": v(4.65, -11.9) * mm, "end": v(4.6, -11.9) * mm});
            skLineSegment(sketch, "E833", {"start": v(4.6, -11.9) * mm, "end": v(4.53, -11.9) * mm});
            skLineSegment(sketch, "E834", {"start": v(4.53, -11.9) * mm, "end": v(4.47, -11.88) * mm});
            skLineSegment(sketch, "E835", {"start": v(4.47, -11.88) * mm, "end": v(4.41, -11.87) * mm});
            skLineSegment(sketch, "E836", {"start": v(4.41, -11.87) * mm, "end": v(4.35, -11.86) * mm});
            skLineSegment(sketch, "E837", {"start": v(4.35, -11.86) * mm, "end": v(4.3, -11.85) * mm});
            skLineSegment(sketch, "E838", {"start": v(4.3, -11.85) * mm, "end": v(4.24, -11.83) * mm});
            skLineSegment(sketch, "E839", {"start": v(4.24, -11.83) * mm, "end": v(3.98, -11.72) * mm});
            skLineSegment(sketch, "E840", {"start": v(3.98, -11.72) * mm, "end": v(3.92, -11.68) * mm});
            skLineSegment(sketch, "E841", {"start": v(3.92, -11.68) * mm, "end": v(3.89, -11.66) * mm});
            skLineSegment(sketch, "E842", {"start": v(3.89, -11.66) * mm, "end": v(3.86, -11.63) * mm});
            skLineSegment(sketch, "E843", {"start": v(3.86, -11.63) * mm, "end": v(3.83, -11.6) * mm});
            skLineSegment(sketch, "E844", {"start": v(3.83, -11.6) * mm, "end": v(3.82, -11.58) * mm});
            skLineSegment(sketch, "E845", {"start": v(3.82, -11.58) * mm, "end": v(3.81, -11.56) * mm});
            skLineSegment(sketch, "E846", {"start": v(3.81, -11.56) * mm, "end": v(3.8, -11.54) * mm});
            skLineSegment(sketch, "E847", {"start": v(3.8, -11.54) * mm, "end": v(3.8, -11.52) * mm});
            skLineSegment(sketch, "E848", {"start": v(3.8, -11.52) * mm, "end": v(3.79, -11.5) * mm});
            skLineSegment(sketch, "E849", {"start": v(3.79, -11.5) * mm, "end": v(3.78, -11.48) * mm});
            skLineSegment(sketch, "E850", {"start": v(3.78, -11.48) * mm, "end": v(3.78, -11.46) * mm});
            skLineSegment(sketch, "E851", {"start": v(3.78, -11.46) * mm, "end": v(3.74, -10.04) * mm});
            skSolve(sketch);
        }
        {
            var Q0;
            Q0=makeQuery(id+"F3.imprint","IMPRINT",FACE,{"disambiguationData":[TD([[makeQuery(id+"F3.imprint","IMPRINT",EDGE,{"derivedFrom":sQuery(id+"F3.wireOp",EDGE,"E8")}),-1.0]])]});
            var Q1;
            Q1=makeQuery(id+"F3.imprint","IMPRINT",FACE,{"disambiguationData":[TD([[makeQuery(id+"F3.imprint","IMPRINT",EDGE,{"derivedFrom":sQuery(id+"F3.wireOp",EDGE,"E372")}),-1.0]])]});
            var Q2;
            Q2=makeQuery(id+"F3.imprint","IMPRINT",FACE,{"disambiguationData":[TD([[makeQuery(id+"F3.imprint","IMPRINT",EDGE,{"derivedFrom":sQuery(id+"F3.wireOp",EDGE,"E448")}),-1.0]])]});
            var Q3;
            Q3=makeQuery(id+"F3.imprint","IMPRINT",FACE,{"disambiguationData":[TD([[makeQuery(id+"F3.imprint","IMPRINT",EDGE,{"derivedFrom":sQuery(id+"F3.wireOp",EDGE,"E528")}),-1.0]])]});
            var Q4;
            Q4=makeQuery(id+"F3.imprint","IMPRINT",FACE,{"disambiguationData":[TD([[makeQuery(id+"F3.imprint","IMPRINT",EDGE,{"derivedFrom":sQuery(id+"F3.wireOp",EDGE,"E616")}),-1.0]])]});
            var Q5;
            Q5=makeQuery(id+"F3.imprint","IMPRINT",FACE,{"disambiguationData":[TD([[makeQuery(id+"F3.imprint","IMPRINT",EDGE,{"derivedFrom":sQuery(id+"F3.wireOp",EDGE,"E808")}),-1.0]])]});
            var Q6;
            Q6=makeQuery(id+"F3.imprint","IMPRINT",FACE,{"disambiguationData":[TD([[makeQuery(id+"F3.imprint","IMPRINT",EDGE,{"derivedFrom":sQuery(id+"F3.wireOp",EDGE,"E752")}),-1.0]])]});
            var Q7;
            Q7=makeQuery(id+"F3.imprint","IMPRINT",FACE,{"disambiguationData":[TD([[makeQuery(id+"F3.imprint","IMPRINT",EDGE,{"derivedFrom":sQuery(id+"F3.wireOp",EDGE,"E703")}),-1.0]])]});
            var Q8;
            Q8=makeQuery(id+"F3.imprint","IMPRINT",FACE,{"disambiguationData":[TD([[makeQuery(id+"F3.imprint","IMPRINT",EDGE,{"derivedFrom":sQuery(id+"F3.wireOp",EDGE,"E657")}),-1.0]])]});
            var Q9;
            Q9=makeQuery(id+"F3.imprint","IMPRINT",FACE,{"disambiguationData":[TD([[makeQuery(id+"F3.imprint","IMPRINT",EDGE,{"derivedFrom":sQuery(id+"F3.wireOp",EDGE,"E562")}),-1.0]])]});
            var Q10;
            Q10=makeQuery(id+"F3.imprint","IMPRINT",FACE,{"disambiguationData":[TD([[makeQuery(id+"F3.imprint","IMPRINT",EDGE,{"derivedFrom":sQuery(id+"F3.wireOp",EDGE,"E479")}),-1.0]])]});
            var Q11;
            Q11=makeQuery(id+"F3.imprint","IMPRINT",FACE,{"disambiguationData":[TD([[makeQuery(id+"F3.imprint","IMPRINT",EDGE,{"derivedFrom":sQuery(id+"F3.wireOp",EDGE,"E417")}),-1.0]])]});
            var Q12;
            Q12=makeQuery(id+"F3.imprint","IMPRINT",FACE,{"disambiguationData":[TD([[makeQuery(id+"F3.imprint","IMPRINT",EDGE,{"derivedFrom":sQuery(id+"F3.wireOp",EDGE,"E328")}),-1.0]])]});
            extrude(context, id + "F4", {"entities" : qUnion([Q0, Q1, Q2, Q3, Q4, Q5, Q6, Q7, Q8, Q9, Q10, Q11, Q12]), "operationType" : NewBodyOperationType.ADD, "depth" : 4 * mm});
        }
        {
            var Q0;
            Q0=makeQuery(id+"F1.opExtrude","SWEPT_EDGE",EDGE,{"disambiguationData":[OSD([sQuery(id+"F0.wireOp",EDGE,"E5.MirrorCS"),sQuery(id+"F0.wireOp",EDGE,"E7.MirrorCS")])]});
            var Q1;
            Q1=makeQuery(id+"F1.opExtrude","SWEPT_EDGE",EDGE,{"disambiguationData":[OSD([sQuery(id+"F0.wireOp",EDGE,"E2"),sQuery(id+"F0.wireOp",EDGE,"E3")])]});
            fillet(context, id + "F5", {"entities" : qUnion([Q0, Q1]), "radius" : 3 * mm, "tangentPropagation" : true, "allowEdgeOverflow" : false});
        }
    });
